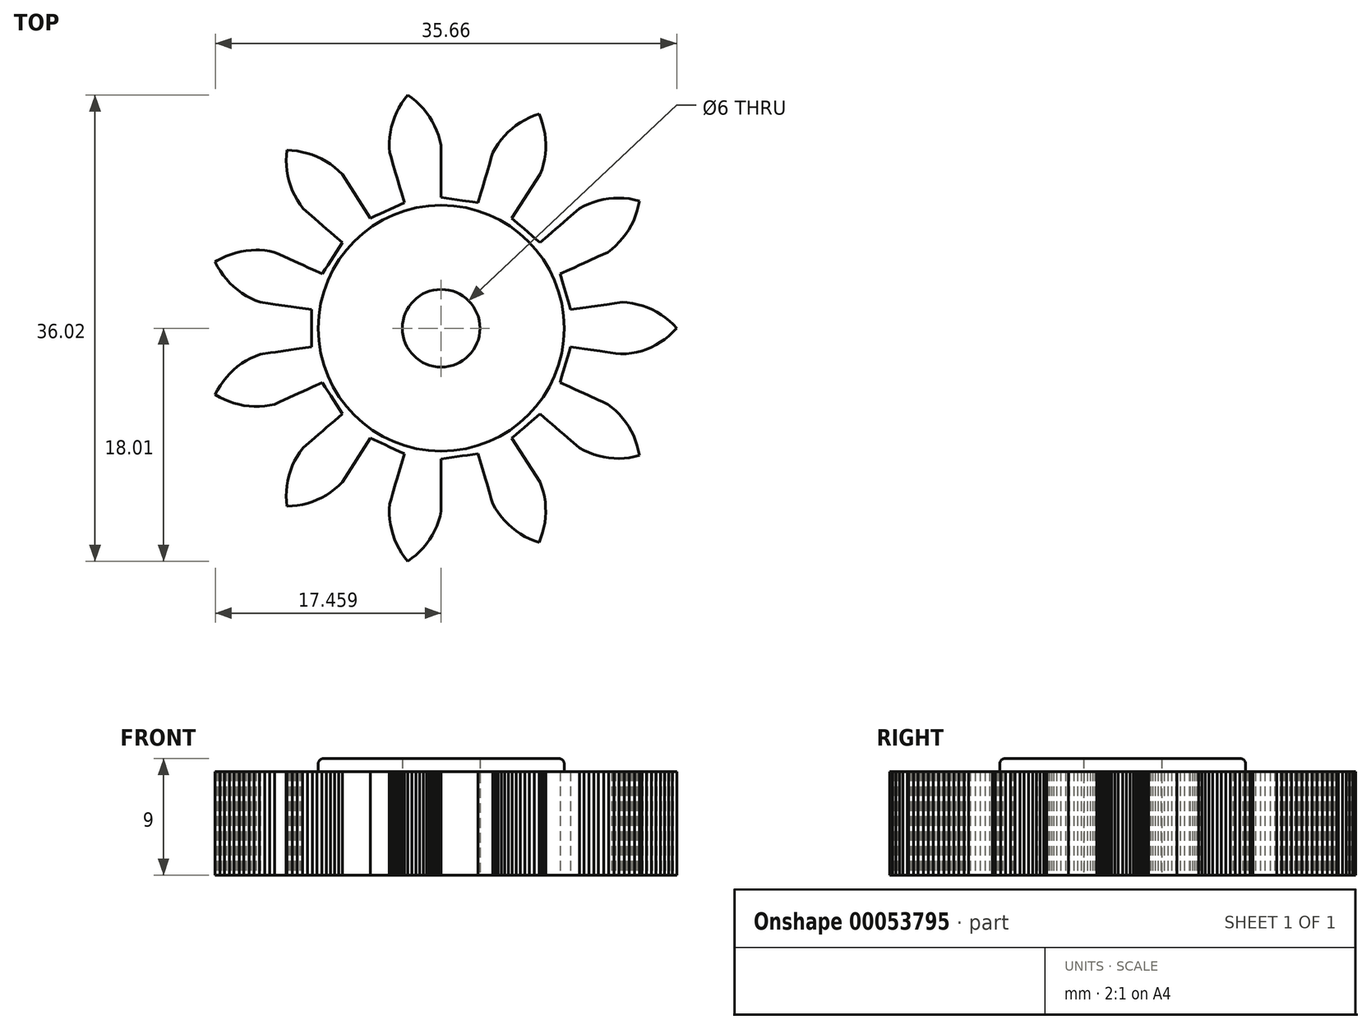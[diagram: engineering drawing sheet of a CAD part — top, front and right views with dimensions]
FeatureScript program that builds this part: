
annotation { "Feature Type Name" : "Feature", "Feature Type Description" : "" }
export const myFeature = defineFeature(function(context is Context, id is Id, definition is map)
    precondition{}
    {
        {
            var Q0;
            Q0=qCreatedBy(makeId("Top.planeOp"),FACE);
            var sketch = newSketch(context, id + "F0", { "sketchPlane" : qUnion([Q0])});
            skLineSegment(sketch, "E0", {"start": v(7.14, -1.44) * mm, "end": v(7.4, -1.48) * mm});
            skLineSegment(sketch, "E1", {"start": v(7.4, -1.48) * mm, "end": v(7.8, -1.53) * mm});
            skLineSegment(sketch, "E2", {"start": v(7.8, -1.53) * mm, "end": v(8.2, -1.6) * mm});
            skLineSegment(sketch, "E3", {"start": v(8.2, -1.6) * mm, "end": v(8.6, -1.65) * mm});
            skLineSegment(sketch, "E4", {"start": v(8.6, -1.65) * mm, "end": v(9, -1.7) * mm});
            skLineSegment(sketch, "E5", {"start": v(9, -1.7) * mm, "end": v(9.4, -1.76) * mm});
            skLineSegment(sketch, "E6", {"start": v(9.4, -1.76) * mm, "end": v(9.8, -1.82) * mm});
            skLineSegment(sketch, "E7", {"start": v(9.8, -1.82) * mm, "end": v(10.2, -1.88) * mm});
            skLineSegment(sketch, "E8", {"start": v(10.2, -1.88) * mm, "end": v(10.6, -1.94) * mm});
            skLineSegment(sketch, "E9", {"start": v(10.6, -1.94) * mm, "end": v(11, -2) * mm});
            skLineSegment(sketch, "E10", {"start": v(11, -2) * mm, "end": v(11.46, -1.99) * mm});
            skLineSegment(sketch, "E11", {"start": v(11.46, -1.99) * mm, "end": v(11.86, -1.93) * mm});
            skLineSegment(sketch, "E12", {"start": v(11.86, -1.93) * mm, "end": v(12.24, -1.86) * mm});
            skLineSegment(sketch, "E13", {"start": v(12.24, -1.86) * mm, "end": v(12.64, -1.75) * mm});
            skLineSegment(sketch, "E14", {"start": v(12.64, -1.75) * mm, "end": v(13, -1.62) * mm});
            skLineSegment(sketch, "E15", {"start": v(13, -1.62) * mm, "end": v(13.38, -1.46) * mm});
            skLineSegment(sketch, "E16", {"start": v(13.38, -1.46) * mm, "end": v(13.73, -1.29) * mm});
            skLineSegment(sketch, "E17", {"start": v(13.73, -1.29) * mm, "end": v(14.08, -1.08) * mm});
            skLineSegment(sketch, "E18", {"start": v(14.08, -1.08) * mm, "end": v(14.4, -0.86) * mm});
            skLineSegment(sketch, "E19", {"start": v(14.4, -0.86) * mm, "end": v(14.72, -0.6) * mm});
            skLineSegment(sketch, "E20", {"start": v(14.72, -0.6) * mm, "end": v(15, -0.35) * mm});
            skLineSegment(sketch, "E21", {"start": v(15, -0.35) * mm, "end": v(15.3, -0.05) * mm});
            skLineSegment(sketch, "E22", {"start": v(15.3, -0.05) * mm, "end": v(15.34, 0) * mm});
            skLineSegment(sketch, "E23", {"start": v(15.34, 0) * mm, "end": v(15.05, 0.3) * mm});
            skLineSegment(sketch, "E24", {"start": v(15.05, 0.3) * mm, "end": v(14.77, 0.56) * mm});
            skLineSegment(sketch, "E25", {"start": v(14.77, 0.56) * mm, "end": v(14.45, 0.82) * mm});
            skLineSegment(sketch, "E26", {"start": v(14.45, 0.82) * mm, "end": v(14.14, 1.04) * mm});
            skLineSegment(sketch, "E27", {"start": v(14.14, 1.04) * mm, "end": v(13.78, 1.25) * mm});
            skLineSegment(sketch, "E28", {"start": v(13.78, 1.25) * mm, "end": v(13.44, 1.43) * mm});
            skLineSegment(sketch, "E29", {"start": v(13.44, 1.43) * mm, "end": v(13.07, 1.6) * mm});
            skLineSegment(sketch, "E30", {"start": v(13.07, 1.6) * mm, "end": v(12.7, 1.73) * mm});
            skLineSegment(sketch, "E31", {"start": v(12.7, 1.73) * mm, "end": v(12.3, 1.84) * mm});
            skLineSegment(sketch, "E32", {"start": v(12.3, 1.84) * mm, "end": v(11.93, 1.92) * mm});
            skLineSegment(sketch, "E33", {"start": v(11.93, 1.92) * mm, "end": v(11.52, 1.98) * mm});
            skLineSegment(sketch, "E34", {"start": v(11.52, 1.98) * mm, "end": v(11.14, 2.01) * mm});
            skLineSegment(sketch, "E35", {"start": v(11.14, 2.01) * mm, "end": v(10.74, 1.96) * mm});
            skLineSegment(sketch, "E36", {"start": v(10.74, 1.96) * mm, "end": v(10.34, 1.9) * mm});
            skLineSegment(sketch, "E37", {"start": v(10.34, 1.9) * mm, "end": v(9.94, 1.84) * mm});
            skLineSegment(sketch, "E38", {"start": v(9.94, 1.84) * mm, "end": v(9.54, 1.78) * mm});
            skLineSegment(sketch, "E39", {"start": v(9.54, 1.78) * mm, "end": v(9.14, 1.73) * mm});
            skLineSegment(sketch, "E40", {"start": v(9.14, 1.73) * mm, "end": v(8.74, 1.67) * mm});
            skLineSegment(sketch, "E41", {"start": v(8.74, 1.67) * mm, "end": v(8.34, 1.61) * mm});
            skLineSegment(sketch, "E42", {"start": v(8.34, 1.61) * mm, "end": v(7.94, 1.55) * mm});
            skLineSegment(sketch, "E43", {"start": v(7.94, 1.55) * mm, "end": v(7.54, 1.5) * mm});
            skLineSegment(sketch, "E44", {"start": v(7.54, 1.5) * mm, "end": v(7.14, 1.44) * mm});
            skLineSegment(sketch, "E45", {"start": v(7.14, 1.44) * mm, "end": v(7.02, 1.83) * mm});
            skLineSegment(sketch, "E46", {"start": v(7.02, 1.83) * mm, "end": v(6.9, 2.23) * mm});
            skLineSegment(sketch, "E47", {"start": v(6.9, 2.23) * mm, "end": v(6.8, 2.62) * mm});
            skLineSegment(sketch, "E48", {"start": v(6.8, 2.62) * mm, "end": v(6.68, 3.01) * mm});
            skLineSegment(sketch, "E49", {"start": v(6.68, 3.01) * mm, "end": v(6.56, 3.4) * mm});
            skLineSegment(sketch, "E50", {"start": v(6.56, 3.4) * mm, "end": v(6.45, 3.8) * mm});
            skLineSegment(sketch, "E51", {"start": v(6.45, 3.8) * mm, "end": v(6.33, 4.2) * mm});
            skLineSegment(sketch, "E52", {"start": v(6.33, 4.2) * mm, "end": v(6.7, 4.36) * mm});
            skLineSegment(sketch, "E53", {"start": v(6.7, 4.36) * mm, "end": v(7.06, 4.53) * mm});
            skLineSegment(sketch, "E54", {"start": v(7.06, 4.53) * mm, "end": v(7.43, 4.7) * mm});
            skLineSegment(sketch, "E55", {"start": v(7.43, 4.7) * mm, "end": v(7.8, 4.87) * mm});
            skLineSegment(sketch, "E56", {"start": v(7.8, 4.87) * mm, "end": v(8.17, 5.04) * mm});
            skLineSegment(sketch, "E57", {"start": v(8.17, 5.04) * mm, "end": v(8.53, 5.2) * mm});
            skLineSegment(sketch, "E58", {"start": v(8.53, 5.2) * mm, "end": v(8.9, 5.37) * mm});
            skLineSegment(sketch, "E59", {"start": v(8.9, 5.37) * mm, "end": v(9.27, 5.54) * mm});
            skLineSegment(sketch, "E60", {"start": v(9.27, 5.54) * mm, "end": v(9.64, 5.7) * mm});
            skLineSegment(sketch, "E61", {"start": v(9.64, 5.7) * mm, "end": v(10, 5.87) * mm});
            skLineSegment(sketch, "E62", {"start": v(10, 5.87) * mm, "end": v(10.33, 6.13) * mm});
            skLineSegment(sketch, "E63", {"start": v(10.33, 6.13) * mm, "end": v(10.62, 6.38) * mm});
            skLineSegment(sketch, "E64", {"start": v(10.62, 6.38) * mm, "end": v(10.9, 6.67) * mm});
            skLineSegment(sketch, "E65", {"start": v(10.9, 6.67) * mm, "end": v(11.17, 6.96) * mm});
            skLineSegment(sketch, "E66", {"start": v(11.17, 6.96) * mm, "end": v(11.41, 7.29) * mm});
            skLineSegment(sketch, "E67", {"start": v(11.41, 7.29) * mm, "end": v(11.63, 7.6) * mm});
            skLineSegment(sketch, "E68", {"start": v(11.63, 7.6) * mm, "end": v(11.83, 7.97) * mm});
            skLineSegment(sketch, "E69", {"start": v(11.83, 7.97) * mm, "end": v(12, 8.31) * mm});
            skLineSegment(sketch, "E70", {"start": v(12, 8.31) * mm, "end": v(12.15, 8.7) * mm});
            skLineSegment(sketch, "E71", {"start": v(12.15, 8.7) * mm, "end": v(12.28, 9.06) * mm});
            skLineSegment(sketch, "E72", {"start": v(12.28, 9.06) * mm, "end": v(12.38, 9.46) * mm});
            skLineSegment(sketch, "E73", {"start": v(12.38, 9.46) * mm, "end": v(12.45, 9.84) * mm});
            skLineSegment(sketch, "E74", {"start": v(12.45, 9.84) * mm, "end": v(12.05, 9.94) * mm});
            skLineSegment(sketch, "E75", {"start": v(12.05, 9.94) * mm, "end": v(11.67, 10) * mm});
            skLineSegment(sketch, "E76", {"start": v(11.67, 10) * mm, "end": v(11.26, 10.05) * mm});
            skLineSegment(sketch, "E77", {"start": v(11.26, 10.05) * mm, "end": v(10.88, 10.06) * mm});
            skLineSegment(sketch, "E78", {"start": v(10.88, 10.06) * mm, "end": v(10.47, 10.05) * mm});
            skLineSegment(sketch, "E79", {"start": v(10.47, 10.05) * mm, "end": v(10.08, 10.02) * mm});
            skLineSegment(sketch, "E80", {"start": v(10.08, 10.02) * mm, "end": v(9.67, 9.95) * mm});
            skLineSegment(sketch, "E81", {"start": v(9.67, 9.95) * mm, "end": v(9.3, 9.87) * mm});
            skLineSegment(sketch, "E82", {"start": v(9.3, 9.87) * mm, "end": v(8.9, 9.75) * mm});
            skLineSegment(sketch, "E83", {"start": v(8.9, 9.75) * mm, "end": v(8.54, 9.61) * mm});
            skLineSegment(sketch, "E84", {"start": v(8.54, 9.61) * mm, "end": v(8.17, 9.44) * mm});
            skLineSegment(sketch, "E85", {"start": v(8.17, 9.44) * mm, "end": v(7.83, 9.26) * mm});
            skLineSegment(sketch, "E86", {"start": v(7.83, 9.26) * mm, "end": v(7.52, 9) * mm});
            skLineSegment(sketch, "E87", {"start": v(7.52, 9) * mm, "end": v(7.22, 8.73) * mm});
            skLineSegment(sketch, "E88", {"start": v(7.22, 8.73) * mm, "end": v(6.91, 8.47) * mm});
            skLineSegment(sketch, "E89", {"start": v(6.91, 8.47) * mm, "end": v(6.6, 8.2) * mm});
            skLineSegment(sketch, "E90", {"start": v(6.6, 8.2) * mm, "end": v(6.3, 7.94) * mm});
            skLineSegment(sketch, "E91", {"start": v(6.3, 7.94) * mm, "end": v(6, 7.67) * mm});
            skLineSegment(sketch, "E92", {"start": v(6, 7.67) * mm, "end": v(5.7, 7.4) * mm});
            skLineSegment(sketch, "E93", {"start": v(5.7, 7.4) * mm, "end": v(5.39, 7.15) * mm});
            skLineSegment(sketch, "E94", {"start": v(5.39, 7.15) * mm, "end": v(5.08, 6.88) * mm});
            skLineSegment(sketch, "E95", {"start": v(5.08, 6.88) * mm, "end": v(4.77, 6.62) * mm});
            skLineSegment(sketch, "E96", {"start": v(4.77, 6.62) * mm, "end": v(4.46, 6.88) * mm});
            skLineSegment(sketch, "E97", {"start": v(4.46, 6.88) * mm, "end": v(4.15, 7.15) * mm});
            skLineSegment(sketch, "E98", {"start": v(4.15, 7.15) * mm, "end": v(3.84, 7.42) * mm});
            skLineSegment(sketch, "E99", {"start": v(3.84, 7.42) * mm, "end": v(3.53, 7.7) * mm});
            skLineSegment(sketch, "E100", {"start": v(3.53, 7.7) * mm, "end": v(3.22, 7.96) * mm});
            skLineSegment(sketch, "E101", {"start": v(3.22, 7.96) * mm, "end": v(2.91, 8.23) * mm});
            skLineSegment(sketch, "E102", {"start": v(2.91, 8.23) * mm, "end": v(2.6, 8.5) * mm});
            skLineSegment(sketch, "E103", {"start": v(2.6, 8.5) * mm, "end": v(2.82, 8.84) * mm});
            skLineSegment(sketch, "E104", {"start": v(2.82, 8.84) * mm, "end": v(3.04, 9.18) * mm});
            skLineSegment(sketch, "E105", {"start": v(3.04, 9.18) * mm, "end": v(3.26, 9.52) * mm});
            skLineSegment(sketch, "E106", {"start": v(3.26, 9.52) * mm, "end": v(3.48, 9.86) * mm});
            skLineSegment(sketch, "E107", {"start": v(3.48, 9.86) * mm, "end": v(3.7, 10.2) * mm});
            skLineSegment(sketch, "E108", {"start": v(3.7, 10.2) * mm, "end": v(3.91, 10.54) * mm});
            skLineSegment(sketch, "E109", {"start": v(3.91, 10.54) * mm, "end": v(4.13, 10.88) * mm});
            skLineSegment(sketch, "E110", {"start": v(4.13, 10.88) * mm, "end": v(4.35, 11.22) * mm});
            skLineSegment(sketch, "E111", {"start": v(4.35, 11.22) * mm, "end": v(4.57, 11.56) * mm});
            skLineSegment(sketch, "E112", {"start": v(4.57, 11.56) * mm, "end": v(4.79, 11.9) * mm});
            skLineSegment(sketch, "E113", {"start": v(4.79, 11.9) * mm, "end": v(4.92, 12.28) * mm});
            skLineSegment(sketch, "E114", {"start": v(4.92, 12.28) * mm, "end": v(5.03, 12.65) * mm});
            skLineSegment(sketch, "E115", {"start": v(5.03, 12.65) * mm, "end": v(5.12, 13.06) * mm});
            skLineSegment(sketch, "E116", {"start": v(5.12, 13.06) * mm, "end": v(5.18, 13.44) * mm});
            skLineSegment(sketch, "E117", {"start": v(5.18, 13.44) * mm, "end": v(5.2, 13.85) * mm});
            skLineSegment(sketch, "E118", {"start": v(5.2, 13.85) * mm, "end": v(5.21, 14.23) * mm});
            skLineSegment(sketch, "E119", {"start": v(5.21, 14.23) * mm, "end": v(5.2, 14.64) * mm});
            skLineSegment(sketch, "E120", {"start": v(5.2, 14.64) * mm, "end": v(5.15, 15.03) * mm});
            skLineSegment(sketch, "E121", {"start": v(5.15, 15.03) * mm, "end": v(5.07, 15.43) * mm});
            skLineSegment(sketch, "E122", {"start": v(5.07, 15.43) * mm, "end": v(4.97, 15.8) * mm});
            skLineSegment(sketch, "E123", {"start": v(4.97, 15.8) * mm, "end": v(4.84, 16.2) * mm});
            skLineSegment(sketch, "E124", {"start": v(4.84, 16.2) * mm, "end": v(4.7, 16.55) * mm});
            skLineSegment(sketch, "E125", {"start": v(4.7, 16.55) * mm, "end": v(4.31, 16.42) * mm});
            skLineSegment(sketch, "E126", {"start": v(4.31, 16.42) * mm, "end": v(3.95, 16.27) * mm});
            skLineSegment(sketch, "E127", {"start": v(3.95, 16.27) * mm, "end": v(3.59, 16.09) * mm});
            skLineSegment(sketch, "E128", {"start": v(3.59, 16.09) * mm, "end": v(3.25, 15.9) * mm});
            skLineSegment(sketch, "E129", {"start": v(3.25, 15.9) * mm, "end": v(2.92, 15.66) * mm});
            skLineSegment(sketch, "E130", {"start": v(2.92, 15.66) * mm, "end": v(2.6, 15.42) * mm});
            skLineSegment(sketch, "E131", {"start": v(2.6, 15.42) * mm, "end": v(2.3, 15.15) * mm});
            skLineSegment(sketch, "E132", {"start": v(2.3, 15.15) * mm, "end": v(2.03, 14.87) * mm});
            skLineSegment(sketch, "E133", {"start": v(2.03, 14.87) * mm, "end": v(1.77, 14.56) * mm});
            skLineSegment(sketch, "E134", {"start": v(1.77, 14.56) * mm, "end": v(1.53, 14.25) * mm});
            skLineSegment(sketch, "E135", {"start": v(1.53, 14.25) * mm, "end": v(1.31, 13.9) * mm});
            skLineSegment(sketch, "E136", {"start": v(1.31, 13.9) * mm, "end": v(1.12, 13.57) * mm});
            skLineSegment(sketch, "E137", {"start": v(1.12, 13.57) * mm, "end": v(1.01, 13.18) * mm});
            skLineSegment(sketch, "E138", {"start": v(1.01, 13.18) * mm, "end": v(0.9, 12.8) * mm});
            skLineSegment(sketch, "E139", {"start": v(0.9, 12.8) * mm, "end": v(0.78, 12.4) * mm});
            skLineSegment(sketch, "E140", {"start": v(0.78, 12.4) * mm, "end": v(0.67, 12.02) * mm});
            skLineSegment(sketch, "E141", {"start": v(0.67, 12.02) * mm, "end": v(0.55, 11.63) * mm});
            skLineSegment(sketch, "E142", {"start": v(0.55, 11.63) * mm, "end": v(0.44, 11.24) * mm});
            skLineSegment(sketch, "E143", {"start": v(0.44, 11.24) * mm, "end": v(0.33, 10.86) * mm});
            skLineSegment(sketch, "E144", {"start": v(0.33, 10.86) * mm, "end": v(0.21, 10.47) * mm});
            skLineSegment(sketch, "E145", {"start": v(0.21, 10.47) * mm, "end": v(0.1, 10.08) * mm});
            skLineSegment(sketch, "E146", {"start": v(0.1, 10.08) * mm, "end": v(-0.01, 9.7) * mm});
            skLineSegment(sketch, "E147", {"start": v(-0.01, 9.7) * mm, "end": v(-0.42, 9.75) * mm});
            skLineSegment(sketch, "E148", {"start": v(-0.42, 9.75) * mm, "end": v(-0.83, 9.81) * mm});
            skLineSegment(sketch, "E149", {"start": v(-0.83, 9.81) * mm, "end": v(-1.23, 9.87) * mm});
            skLineSegment(sketch, "E150", {"start": v(-1.23, 9.87) * mm, "end": v(-1.64, 9.93) * mm});
            skLineSegment(sketch, "E151", {"start": v(-1.64, 9.93) * mm, "end": v(-2.05, 9.99) * mm});
            skLineSegment(sketch, "E152", {"start": v(-2.05, 9.99) * mm, "end": v(-2.45, 10.04) * mm});
            skLineSegment(sketch, "E153", {"start": v(-2.45, 10.04) * mm, "end": v(-2.86, 10.1) * mm});
            skLineSegment(sketch, "E154", {"start": v(-2.86, 10.1) * mm, "end": v(-2.86, 10.5) * mm});
            skLineSegment(sketch, "E155", {"start": v(-2.86, 10.5) * mm, "end": v(-2.86, 10.91) * mm});
            skLineSegment(sketch, "E156", {"start": v(-2.86, 10.91) * mm, "end": v(-2.86, 11.31) * mm});
            skLineSegment(sketch, "E157", {"start": v(-2.86, 11.31) * mm, "end": v(-2.86, 11.72) * mm});
            skLineSegment(sketch, "E158", {"start": v(-2.86, 11.72) * mm, "end": v(-2.86, 12.12) * mm});
            skLineSegment(sketch, "E159", {"start": v(-2.86, 12.12) * mm, "end": v(-2.86, 12.53) * mm});
            skLineSegment(sketch, "E160", {"start": v(-2.86, 12.53) * mm, "end": v(-2.86, 12.93) * mm});
            skLineSegment(sketch, "E161", {"start": v(-2.86, 12.93) * mm, "end": v(-2.86, 13.33) * mm});
            skLineSegment(sketch, "E162", {"start": v(-2.86, 13.33) * mm, "end": v(-2.86, 13.74) * mm});
            skLineSegment(sketch, "E163", {"start": v(-2.86, 13.74) * mm, "end": v(-2.86, 14.14) * mm});
            skLineSegment(sketch, "E164", {"start": v(-2.86, 14.14) * mm, "end": v(-2.95, 14.54) * mm});
            skLineSegment(sketch, "E165", {"start": v(-2.95, 14.54) * mm, "end": v(-3.06, 14.91) * mm});
            skLineSegment(sketch, "E166", {"start": v(-3.06, 14.91) * mm, "end": v(-3.2, 15.3) * mm});
            skLineSegment(sketch, "E167", {"start": v(-3.2, 15.3) * mm, "end": v(-3.36, 15.65) * mm});
            skLineSegment(sketch, "E168", {"start": v(-3.36, 15.65) * mm, "end": v(-3.56, 16.01) * mm});
            skLineSegment(sketch, "E169", {"start": v(-3.56, 16.01) * mm, "end": v(-3.76, 16.34) * mm});
            skLineSegment(sketch, "E170", {"start": v(-3.76, 16.34) * mm, "end": v(-4, 16.67) * mm});
            skLineSegment(sketch, "E171", {"start": v(-4, 16.67) * mm, "end": v(-4.25, 16.97) * mm});
            skLineSegment(sketch, "E172", {"start": v(-4.25, 16.97) * mm, "end": v(-4.53, 17.27) * mm});
            skLineSegment(sketch, "E173", {"start": v(-4.53, 17.27) * mm, "end": v(-4.82, 17.53) * mm});
            skLineSegment(sketch, "E174", {"start": v(-4.82, 17.53) * mm, "end": v(-5.14, 17.79) * mm});
            skLineSegment(sketch, "E175", {"start": v(-5.14, 17.79) * mm, "end": v(-5.45, 18.01) * mm});
            skLineSegment(sketch, "E176", {"start": v(-5.45, 18.01) * mm, "end": v(-5.7, 17.7) * mm});
            skLineSegment(sketch, "E177", {"start": v(-5.7, 17.7) * mm, "end": v(-5.92, 17.37) * mm});
            skLineSegment(sketch, "E178", {"start": v(-5.92, 17.37) * mm, "end": v(-6.13, 17.02) * mm});
            skLineSegment(sketch, "E179", {"start": v(-6.13, 17.02) * mm, "end": v(-6.3, 16.68) * mm});
            skLineSegment(sketch, "E180", {"start": v(-6.3, 16.68) * mm, "end": v(-6.47, 16.3) * mm});
            skLineSegment(sketch, "E181", {"start": v(-6.47, 16.3) * mm, "end": v(-6.6, 15.93) * mm});
            skLineSegment(sketch, "E182", {"start": v(-6.6, 15.93) * mm, "end": v(-6.7, 15.54) * mm});
            skLineSegment(sketch, "E183", {"start": v(-6.7, 15.54) * mm, "end": v(-6.79, 15.16) * mm});
            skLineSegment(sketch, "E184", {"start": v(-6.79, 15.16) * mm, "end": v(-6.84, 14.75) * mm});
            skLineSegment(sketch, "E185", {"start": v(-6.84, 14.75) * mm, "end": v(-6.87, 14.37) * mm});
            skLineSegment(sketch, "E186", {"start": v(-6.87, 14.37) * mm, "end": v(-6.87, 13.96) * mm});
            skLineSegment(sketch, "E187", {"start": v(-6.87, 13.96) * mm, "end": v(-6.84, 13.57) * mm});
            skLineSegment(sketch, "E188", {"start": v(-6.84, 13.57) * mm, "end": v(-6.73, 13.18) * mm});
            skLineSegment(sketch, "E189", {"start": v(-6.73, 13.18) * mm, "end": v(-6.62, 12.8) * mm});
            skLineSegment(sketch, "E190", {"start": v(-6.62, 12.8) * mm, "end": v(-6.5, 12.4) * mm});
            skLineSegment(sketch, "E191", {"start": v(-6.5, 12.4) * mm, "end": v(-6.39, 12.02) * mm});
            skLineSegment(sketch, "E192", {"start": v(-6.39, 12.02) * mm, "end": v(-6.28, 11.63) * mm});
            skLineSegment(sketch, "E193", {"start": v(-6.28, 11.63) * mm, "end": v(-6.16, 11.24) * mm});
            skLineSegment(sketch, "E194", {"start": v(-6.16, 11.24) * mm, "end": v(-6.05, 10.86) * mm});
            skLineSegment(sketch, "E195", {"start": v(-6.05, 10.86) * mm, "end": v(-5.93, 10.47) * mm});
            skLineSegment(sketch, "E196", {"start": v(-5.93, 10.47) * mm, "end": v(-5.82, 10.08) * mm});
            skLineSegment(sketch, "E197", {"start": v(-5.82, 10.08) * mm, "end": v(-5.7, 9.7) * mm});
            skLineSegment(sketch, "E198", {"start": v(-5.7, 9.7) * mm, "end": v(-6.08, 9.52) * mm});
            skLineSegment(sketch, "E199", {"start": v(-6.08, 9.52) * mm, "end": v(-6.45, 9.35) * mm});
            skLineSegment(sketch, "E200", {"start": v(-6.45, 9.35) * mm, "end": v(-6.83, 9.18) * mm});
            skLineSegment(sketch, "E201", {"start": v(-6.83, 9.18) * mm, "end": v(-7.2, 9.01) * mm});
            skLineSegment(sketch, "E202", {"start": v(-7.2, 9.01) * mm, "end": v(-7.57, 8.84) * mm});
            skLineSegment(sketch, "E203", {"start": v(-7.57, 8.84) * mm, "end": v(-7.95, 8.67) * mm});
            skLineSegment(sketch, "E204", {"start": v(-7.95, 8.67) * mm, "end": v(-8.32, 8.5) * mm});
            skLineSegment(sketch, "E205", {"start": v(-8.32, 8.5) * mm, "end": v(-8.54, 8.84) * mm});
            skLineSegment(sketch, "E206", {"start": v(-8.54, 8.84) * mm, "end": v(-8.76, 9.18) * mm});
            skLineSegment(sketch, "E207", {"start": v(-8.76, 9.18) * mm, "end": v(-8.98, 9.52) * mm});
            skLineSegment(sketch, "E208", {"start": v(-8.98, 9.52) * mm, "end": v(-9.2, 9.86) * mm});
            skLineSegment(sketch, "E209", {"start": v(-9.2, 9.86) * mm, "end": v(-9.41, 10.2) * mm});
            skLineSegment(sketch, "E210", {"start": v(-9.41, 10.2) * mm, "end": v(-9.63, 10.54) * mm});
            skLineSegment(sketch, "E211", {"start": v(-9.63, 10.54) * mm, "end": v(-9.85, 10.88) * mm});
            skLineSegment(sketch, "E212", {"start": v(-9.85, 10.88) * mm, "end": v(-10.07, 11.22) * mm});
            skLineSegment(sketch, "E213", {"start": v(-10.07, 11.22) * mm, "end": v(-10.29, 11.56) * mm});
            skLineSegment(sketch, "E214", {"start": v(-10.29, 11.56) * mm, "end": v(-10.5, 11.9) * mm});
            skLineSegment(sketch, "E215", {"start": v(-10.5, 11.9) * mm, "end": v(-10.8, 12.18) * mm});
            skLineSegment(sketch, "E216", {"start": v(-10.8, 12.18) * mm, "end": v(-11.1, 12.44) * mm});
            skLineSegment(sketch, "E217", {"start": v(-11.1, 12.44) * mm, "end": v(-11.42, 12.68) * mm});
            skLineSegment(sketch, "E218", {"start": v(-11.42, 12.68) * mm, "end": v(-11.75, 12.9) * mm});
            skLineSegment(sketch, "E219", {"start": v(-11.75, 12.9) * mm, "end": v(-12.1, 13.1) * mm});
            skLineSegment(sketch, "E220", {"start": v(-12.1, 13.1) * mm, "end": v(-12.45, 13.26) * mm});
            skLineSegment(sketch, "E221", {"start": v(-12.45, 13.26) * mm, "end": v(-12.84, 13.4) * mm});
            skLineSegment(sketch, "E222", {"start": v(-12.84, 13.4) * mm, "end": v(-13.2, 13.53) * mm});
            skLineSegment(sketch, "E223", {"start": v(-13.2, 13.53) * mm, "end": v(-13.6, 13.62) * mm});
            skLineSegment(sketch, "E224", {"start": v(-13.6, 13.62) * mm, "end": v(-13.98, 13.7) * mm});
            skLineSegment(sketch, "E225", {"start": v(-13.98, 13.7) * mm, "end": v(-14.4, 13.74) * mm});
            skLineSegment(sketch, "E226", {"start": v(-14.4, 13.74) * mm, "end": v(-14.78, 13.75) * mm});
            skLineSegment(sketch, "E227", {"start": v(-14.78, 13.75) * mm, "end": v(-14.82, 13.35) * mm});
            skLineSegment(sketch, "E228", {"start": v(-14.82, 13.35) * mm, "end": v(-14.83, 12.96) * mm});
            skLineSegment(sketch, "E229", {"start": v(-14.83, 12.96) * mm, "end": v(-14.81, 12.55) * mm});
            skLineSegment(sketch, "E230", {"start": v(-14.81, 12.55) * mm, "end": v(-14.78, 12.16) * mm});
            skLineSegment(sketch, "E231", {"start": v(-14.78, 12.16) * mm, "end": v(-14.7, 11.76) * mm});
            skLineSegment(sketch, "E232", {"start": v(-14.7, 11.76) * mm, "end": v(-14.62, 11.38) * mm});
            skLineSegment(sketch, "E233", {"start": v(-14.62, 11.38) * mm, "end": v(-14.5, 11) * mm});
            skLineSegment(sketch, "E234", {"start": v(-14.5, 11) * mm, "end": v(-14.36, 10.63) * mm});
            skLineSegment(sketch, "E235", {"start": v(-14.36, 10.63) * mm, "end": v(-14.18, 10.26) * mm});
            skLineSegment(sketch, "E236", {"start": v(-14.18, 10.26) * mm, "end": v(-14, 9.92) * mm});
            skLineSegment(sketch, "E237", {"start": v(-14, 9.92) * mm, "end": v(-13.78, 9.57) * mm});
            skLineSegment(sketch, "E238", {"start": v(-13.78, 9.57) * mm, "end": v(-13.55, 9.26) * mm});
            skLineSegment(sketch, "E239", {"start": v(-13.55, 9.26) * mm, "end": v(-13.24, 9) * mm});
            skLineSegment(sketch, "E240", {"start": v(-13.24, 9) * mm, "end": v(-12.94, 8.73) * mm});
            skLineSegment(sketch, "E241", {"start": v(-12.94, 8.73) * mm, "end": v(-12.63, 8.47) * mm});
            skLineSegment(sketch, "E242", {"start": v(-12.63, 8.47) * mm, "end": v(-12.33, 8.2) * mm});
            skLineSegment(sketch, "E243", {"start": v(-12.33, 8.2) * mm, "end": v(-12.02, 7.94) * mm});
            skLineSegment(sketch, "E244", {"start": v(-12.02, 7.94) * mm, "end": v(-11.72, 7.67) * mm});
            skLineSegment(sketch, "E245", {"start": v(-11.72, 7.67) * mm, "end": v(-11.41, 7.4) * mm});
            skLineSegment(sketch, "E246", {"start": v(-11.41, 7.4) * mm, "end": v(-11.1, 7.15) * mm});
            skLineSegment(sketch, "E247", {"start": v(-11.1, 7.15) * mm, "end": v(-10.8, 6.88) * mm});
            skLineSegment(sketch, "E248", {"start": v(-10.8, 6.88) * mm, "end": v(-10.5, 6.62) * mm});
            skLineSegment(sketch, "E249", {"start": v(-10.5, 6.62) * mm, "end": v(-10.72, 6.27) * mm});
            skLineSegment(sketch, "E250", {"start": v(-10.72, 6.27) * mm, "end": v(-10.94, 5.93) * mm});
            skLineSegment(sketch, "E251", {"start": v(-10.94, 5.93) * mm, "end": v(-11.16, 5.58) * mm});
            skLineSegment(sketch, "E252", {"start": v(-11.16, 5.58) * mm, "end": v(-11.38, 5.23) * mm});
            skLineSegment(sketch, "E253", {"start": v(-11.38, 5.23) * mm, "end": v(-11.6, 4.89) * mm});
            skLineSegment(sketch, "E254", {"start": v(-11.6, 4.89) * mm, "end": v(-11.83, 4.54) * mm});
            skLineSegment(sketch, "E255", {"start": v(-11.83, 4.54) * mm, "end": v(-12.05, 4.2) * mm});
            skLineSegment(sketch, "E256", {"start": v(-12.05, 4.2) * mm, "end": v(-12.42, 4.36) * mm});
            skLineSegment(sketch, "E257", {"start": v(-12.42, 4.36) * mm, "end": v(-12.79, 4.53) * mm});
            skLineSegment(sketch, "E258", {"start": v(-12.79, 4.53) * mm, "end": v(-13.15, 4.7) * mm});
            skLineSegment(sketch, "E259", {"start": v(-13.15, 4.7) * mm, "end": v(-13.52, 4.87) * mm});
            skLineSegment(sketch, "E260", {"start": v(-13.52, 4.87) * mm, "end": v(-13.89, 5.04) * mm});
            skLineSegment(sketch, "E261", {"start": v(-13.89, 5.04) * mm, "end": v(-14.26, 5.2) * mm});
            skLineSegment(sketch, "E262", {"start": v(-14.26, 5.2) * mm, "end": v(-14.62, 5.37) * mm});
            skLineSegment(sketch, "E263", {"start": v(-14.62, 5.37) * mm, "end": v(-14.99, 5.54) * mm});
            skLineSegment(sketch, "E264", {"start": v(-14.99, 5.54) * mm, "end": v(-15.36, 5.7) * mm});
            skLineSegment(sketch, "E265", {"start": v(-15.36, 5.7) * mm, "end": v(-15.72, 5.87) * mm});
            skLineSegment(sketch, "E266", {"start": v(-15.72, 5.87) * mm, "end": v(-16.13, 5.96) * mm});
            skLineSegment(sketch, "E267", {"start": v(-16.13, 5.96) * mm, "end": v(-16.5, 6.01) * mm});
            skLineSegment(sketch, "E268", {"start": v(-16.5, 6.01) * mm, "end": v(-16.92, 6.04) * mm});
            skLineSegment(sketch, "E269", {"start": v(-16.92, 6.04) * mm, "end": v(-17.15, 6.04) * mm});
            skLineSegment(sketch, "E270", {"start": v(-17.15, 6.04) * mm, "end": v(-17.56, 6.03) * mm});
            skLineSegment(sketch, "E271", {"start": v(-17.56, 6.03) * mm, "end": v(-17.94, 6) * mm});
            skLineSegment(sketch, "E272", {"start": v(-17.94, 6) * mm, "end": v(-18.35, 5.92) * mm});
            skLineSegment(sketch, "E273", {"start": v(-18.35, 5.92) * mm, "end": v(-18.72, 5.83) * mm});
            skLineSegment(sketch, "E274", {"start": v(-18.72, 5.83) * mm, "end": v(-19.11, 5.7) * mm});
            skLineSegment(sketch, "E275", {"start": v(-19.11, 5.7) * mm, "end": v(-19.48, 5.57) * mm});
            skLineSegment(sketch, "E276", {"start": v(-19.48, 5.57) * mm, "end": v(-19.85, 5.4) * mm});
            skLineSegment(sketch, "E277", {"start": v(-19.85, 5.4) * mm, "end": v(-20.19, 5.21) * mm});
            skLineSegment(sketch, "E278", {"start": v(-20.19, 5.21) * mm, "end": v(-20.32, 5.13) * mm});
            skLineSegment(sketch, "E279", {"start": v(-20.32, 5.13) * mm, "end": v(-20.13, 4.76) * mm});
            skLineSegment(sketch, "E280", {"start": v(-20.13, 4.76) * mm, "end": v(-19.94, 4.43) * mm});
            skLineSegment(sketch, "E281", {"start": v(-19.94, 4.43) * mm, "end": v(-19.7, 4.1) * mm});
            skLineSegment(sketch, "E282", {"start": v(-19.7, 4.1) * mm, "end": v(-19.46, 3.79) * mm});
            skLineSegment(sketch, "E283", {"start": v(-19.46, 3.79) * mm, "end": v(-19.18, 3.49) * mm});
            skLineSegment(sketch, "E284", {"start": v(-19.18, 3.49) * mm, "end": v(-18.9, 3.22) * mm});
            skLineSegment(sketch, "E285", {"start": v(-18.9, 3.22) * mm, "end": v(-18.6, 2.96) * mm});
            skLineSegment(sketch, "E286", {"start": v(-18.6, 2.96) * mm, "end": v(-18.28, 2.73) * mm});
            skLineSegment(sketch, "E287", {"start": v(-18.28, 2.73) * mm, "end": v(-17.93, 2.5) * mm});
            skLineSegment(sketch, "E288", {"start": v(-17.93, 2.5) * mm, "end": v(-17.6, 2.32) * mm});
            skLineSegment(sketch, "E289", {"start": v(-17.6, 2.32) * mm, "end": v(-17.22, 2.15) * mm});
            skLineSegment(sketch, "E290", {"start": v(-17.22, 2.15) * mm, "end": v(-16.86, 2.01) * mm});
            skLineSegment(sketch, "E291", {"start": v(-16.86, 2.01) * mm, "end": v(-16.46, 1.96) * mm});
            skLineSegment(sketch, "E292", {"start": v(-16.46, 1.96) * mm, "end": v(-16.06, 1.9) * mm});
            skLineSegment(sketch, "E293", {"start": v(-16.06, 1.9) * mm, "end": v(-15.66, 1.84) * mm});
            skLineSegment(sketch, "E294", {"start": v(-15.66, 1.84) * mm, "end": v(-15.26, 1.78) * mm});
            skLineSegment(sketch, "E295", {"start": v(-15.26, 1.78) * mm, "end": v(-14.86, 1.73) * mm});
            skLineSegment(sketch, "E296", {"start": v(-14.86, 1.73) * mm, "end": v(-14.46, 1.67) * mm});
            skLineSegment(sketch, "E297", {"start": v(-14.46, 1.67) * mm, "end": v(-14.06, 1.61) * mm});
            skLineSegment(sketch, "E298", {"start": v(-14.06, 1.61) * mm, "end": v(-13.66, 1.55) * mm});
            skLineSegment(sketch, "E299", {"start": v(-13.66, 1.55) * mm, "end": v(-13.26, 1.5) * mm});
            skLineSegment(sketch, "E300", {"start": v(-13.26, 1.5) * mm, "end": v(-12.86, 1.44) * mm});
            skLineSegment(sketch, "E301", {"start": v(-12.86, 1.44) * mm, "end": v(-12.86, 1.03) * mm});
            skLineSegment(sketch, "E302", {"start": v(-12.86, 1.03) * mm, "end": v(-12.86, 0.62) * mm});
            skLineSegment(sketch, "E303", {"start": v(-12.86, 0.62) * mm, "end": v(-12.86, 0.2) * mm});
            skLineSegment(sketch, "E304", {"start": v(-12.86, 0.2) * mm, "end": v(-12.86, -0.2) * mm});
            skLineSegment(sketch, "E305", {"start": v(-12.86, -0.2) * mm, "end": v(-12.86, -0.61) * mm});
            skLineSegment(sketch, "E306", {"start": v(-12.86, -0.61) * mm, "end": v(-12.86, -1.02) * mm});
            skLineSegment(sketch, "E307", {"start": v(-12.86, -1.02) * mm, "end": v(-12.86, -1.44) * mm});
            skLineSegment(sketch, "E308", {"start": v(-12.86, -1.44) * mm, "end": v(-13.26, -1.5) * mm});
            skLineSegment(sketch, "E309", {"start": v(-13.26, -1.5) * mm, "end": v(-13.66, -1.55) * mm});
            skLineSegment(sketch, "E310", {"start": v(-13.66, -1.55) * mm, "end": v(-14.06, -1.61) * mm});
            skLineSegment(sketch, "E311", {"start": v(-14.06, -1.61) * mm, "end": v(-14.46, -1.67) * mm});
            skLineSegment(sketch, "E312", {"start": v(-14.46, -1.67) * mm, "end": v(-14.86, -1.73) * mm});
            skLineSegment(sketch, "E313", {"start": v(-14.86, -1.73) * mm, "end": v(-15.26, -1.78) * mm});
            skLineSegment(sketch, "E314", {"start": v(-15.26, -1.78) * mm, "end": v(-15.66, -1.84) * mm});
            skLineSegment(sketch, "E315", {"start": v(-15.66, -1.84) * mm, "end": v(-16.06, -1.9) * mm});
            skLineSegment(sketch, "E316", {"start": v(-16.06, -1.9) * mm, "end": v(-16.46, -1.96) * mm});
            skLineSegment(sketch, "E317", {"start": v(-16.46, -1.96) * mm, "end": v(-16.86, -2.01) * mm});
            skLineSegment(sketch, "E318", {"start": v(-16.86, -2.01) * mm, "end": v(-17.24, -2.16) * mm});
            skLineSegment(sketch, "E319", {"start": v(-17.24, -2.16) * mm, "end": v(-17.6, -2.32) * mm});
            skLineSegment(sketch, "E320", {"start": v(-17.6, -2.32) * mm, "end": v(-17.95, -2.52) * mm});
            skLineSegment(sketch, "E321", {"start": v(-17.95, -2.52) * mm, "end": v(-18.28, -2.73) * mm});
            skLineSegment(sketch, "E322", {"start": v(-18.28, -2.73) * mm, "end": v(-18.6, -2.97) * mm});
            skLineSegment(sketch, "E323", {"start": v(-18.6, -2.97) * mm, "end": v(-18.9, -3.22) * mm});
            skLineSegment(sketch, "E324", {"start": v(-18.9, -3.22) * mm, "end": v(-19.2, -3.5) * mm});
            skLineSegment(sketch, "E325", {"start": v(-19.2, -3.5) * mm, "end": v(-19.46, -3.79) * mm});
            skLineSegment(sketch, "E326", {"start": v(-19.46, -3.79) * mm, "end": v(-19.72, -4.11) * mm});
            skLineSegment(sketch, "E327", {"start": v(-19.72, -4.11) * mm, "end": v(-19.94, -4.43) * mm});
            skLineSegment(sketch, "E328", {"start": v(-19.94, -4.43) * mm, "end": v(-20.14, -4.78) * mm});
            skLineSegment(sketch, "E329", {"start": v(-20.14, -4.78) * mm, "end": v(-20.32, -5.13) * mm});
            skLineSegment(sketch, "E330", {"start": v(-20.32, -5.13) * mm, "end": v(-19.97, -5.33) * mm});
            skLineSegment(sketch, "E331", {"start": v(-19.97, -5.33) * mm, "end": v(-19.62, -5.5) * mm});
            skLineSegment(sketch, "E332", {"start": v(-19.62, -5.5) * mm, "end": v(-19.24, -5.66) * mm});
            skLineSegment(sketch, "E333", {"start": v(-19.24, -5.66) * mm, "end": v(-18.88, -5.79) * mm});
            skLineSegment(sketch, "E334", {"start": v(-18.88, -5.79) * mm, "end": v(-18.48, -5.9) * mm});
            skLineSegment(sketch, "E335", {"start": v(-18.48, -5.9) * mm, "end": v(-18.1, -5.97) * mm});
            skLineSegment(sketch, "E336", {"start": v(-18.1, -5.97) * mm, "end": v(-17.7, -6.02) * mm});
            skLineSegment(sketch, "E337", {"start": v(-17.7, -6.02) * mm, "end": v(-17.3, -6.04) * mm});
            skLineSegment(sketch, "E338", {"start": v(-17.3, -6.04) * mm, "end": v(-16.9, -6.04) * mm});
            skLineSegment(sketch, "E339", {"start": v(-16.9, -6.04) * mm, "end": v(-16.5, -6.01) * mm});
            skLineSegment(sketch, "E340", {"start": v(-16.5, -6.01) * mm, "end": v(-16.1, -5.95) * mm});
            skLineSegment(sketch, "E341", {"start": v(-16.1, -5.95) * mm, "end": v(-15.72, -5.87) * mm});
            skLineSegment(sketch, "E342", {"start": v(-15.72, -5.87) * mm, "end": v(-15.36, -5.7) * mm});
            skLineSegment(sketch, "E343", {"start": v(-15.36, -5.7) * mm, "end": v(-14.99, -5.54) * mm});
            skLineSegment(sketch, "E344", {"start": v(-14.99, -5.54) * mm, "end": v(-14.62, -5.37) * mm});
            skLineSegment(sketch, "E345", {"start": v(-14.62, -5.37) * mm, "end": v(-14.26, -5.2) * mm});
            skLineSegment(sketch, "E346", {"start": v(-14.26, -5.2) * mm, "end": v(-13.89, -5.04) * mm});
            skLineSegment(sketch, "E347", {"start": v(-13.89, -5.04) * mm, "end": v(-13.52, -4.87) * mm});
            skLineSegment(sketch, "E348", {"start": v(-13.52, -4.87) * mm, "end": v(-13.15, -4.7) * mm});
            skLineSegment(sketch, "E349", {"start": v(-13.15, -4.7) * mm, "end": v(-12.79, -4.53) * mm});
            skLineSegment(sketch, "E350", {"start": v(-12.79, -4.53) * mm, "end": v(-12.42, -4.36) * mm});
            skLineSegment(sketch, "E351", {"start": v(-12.42, -4.36) * mm, "end": v(-12.05, -4.2) * mm});
            skLineSegment(sketch, "E352", {"start": v(-12.05, -4.2) * mm, "end": v(-11.83, -4.54) * mm});
            skLineSegment(sketch, "E353", {"start": v(-11.83, -4.54) * mm, "end": v(-11.6, -4.89) * mm});
            skLineSegment(sketch, "E354", {"start": v(-11.6, -4.89) * mm, "end": v(-11.38, -5.23) * mm});
            skLineSegment(sketch, "E355", {"start": v(-11.38, -5.23) * mm, "end": v(-11.16, -5.58) * mm});
            skLineSegment(sketch, "E356", {"start": v(-11.16, -5.58) * mm, "end": v(-10.94, -5.92) * mm});
            skLineSegment(sketch, "E357", {"start": v(-10.94, -5.92) * mm, "end": v(-10.72, -6.27) * mm});
            skLineSegment(sketch, "E358", {"start": v(-10.72, -6.27) * mm, "end": v(-10.5, -6.62) * mm});
            skLineSegment(sketch, "E359", {"start": v(-10.5, -6.62) * mm, "end": v(-10.8, -6.88) * mm});
            skLineSegment(sketch, "E360", {"start": v(-10.8, -6.88) * mm, "end": v(-11.1, -7.15) * mm});
            skLineSegment(sketch, "E361", {"start": v(-11.1, -7.15) * mm, "end": v(-11.41, -7.4) * mm});
            skLineSegment(sketch, "E362", {"start": v(-11.41, -7.4) * mm, "end": v(-11.72, -7.67) * mm});
            skLineSegment(sketch, "E363", {"start": v(-11.72, -7.67) * mm, "end": v(-12.02, -7.94) * mm});
            skLineSegment(sketch, "E364", {"start": v(-12.02, -7.94) * mm, "end": v(-12.33, -8.2) * mm});
            skLineSegment(sketch, "E365", {"start": v(-12.33, -8.2) * mm, "end": v(-12.63, -8.47) * mm});
            skLineSegment(sketch, "E366", {"start": v(-12.63, -8.47) * mm, "end": v(-12.94, -8.73) * mm});
            skLineSegment(sketch, "E367", {"start": v(-12.94, -8.73) * mm, "end": v(-13.24, -9) * mm});
            skLineSegment(sketch, "E368", {"start": v(-13.24, -9) * mm, "end": v(-13.55, -9.26) * mm});
            skLineSegment(sketch, "E369", {"start": v(-13.55, -9.26) * mm, "end": v(-13.79, -9.6) * mm});
            skLineSegment(sketch, "E370", {"start": v(-13.79, -9.6) * mm, "end": v(-14, -9.92) * mm});
            skLineSegment(sketch, "E371", {"start": v(-14, -9.92) * mm, "end": v(-14.2, -10.28) * mm});
            skLineSegment(sketch, "E372", {"start": v(-14.2, -10.28) * mm, "end": v(-14.36, -10.63) * mm});
            skLineSegment(sketch, "E373", {"start": v(-14.36, -10.63) * mm, "end": v(-14.5, -11.01) * mm});
            skLineSegment(sketch, "E374", {"start": v(-14.5, -11.01) * mm, "end": v(-14.62, -11.38) * mm});
            skLineSegment(sketch, "E375", {"start": v(-14.62, -11.38) * mm, "end": v(-14.71, -11.78) * mm});
            skLineSegment(sketch, "E376", {"start": v(-14.71, -11.78) * mm, "end": v(-14.78, -12.16) * mm});
            skLineSegment(sketch, "E377", {"start": v(-14.78, -12.16) * mm, "end": v(-14.82, -12.57) * mm});
            skLineSegment(sketch, "E378", {"start": v(-14.82, -12.57) * mm, "end": v(-14.83, -12.96) * mm});
            skLineSegment(sketch, "E379", {"start": v(-14.83, -12.96) * mm, "end": v(-14.81, -13.37) * mm});
            skLineSegment(sketch, "E380", {"start": v(-14.81, -13.37) * mm, "end": v(-14.78, -13.75) * mm});
            skLineSegment(sketch, "E381", {"start": v(-14.78, -13.75) * mm, "end": v(-14.37, -13.73) * mm});
            skLineSegment(sketch, "E382", {"start": v(-14.37, -13.73) * mm, "end": v(-13.98, -13.7) * mm});
            skLineSegment(sketch, "E383", {"start": v(-13.98, -13.7) * mm, "end": v(-13.58, -13.62) * mm});
            skLineSegment(sketch, "E384", {"start": v(-13.58, -13.62) * mm, "end": v(-13.2, -13.53) * mm});
            skLineSegment(sketch, "E385", {"start": v(-13.2, -13.53) * mm, "end": v(-12.81, -13.4) * mm});
            skLineSegment(sketch, "E386", {"start": v(-12.81, -13.4) * mm, "end": v(-12.45, -13.26) * mm});
            skLineSegment(sketch, "E387", {"start": v(-12.45, -13.26) * mm, "end": v(-12.08, -13.08) * mm});
            skLineSegment(sketch, "E388", {"start": v(-12.08, -13.08) * mm, "end": v(-11.75, -12.9) * mm});
            skLineSegment(sketch, "E389", {"start": v(-11.75, -12.9) * mm, "end": v(-11.4, -12.67) * mm});
            skLineSegment(sketch, "E390", {"start": v(-11.4, -12.67) * mm, "end": v(-11.1, -12.44) * mm});
            skLineSegment(sketch, "E391", {"start": v(-11.1, -12.44) * mm, "end": v(-10.78, -12.17) * mm});
            skLineSegment(sketch, "E392", {"start": v(-10.78, -12.17) * mm, "end": v(-10.5, -11.9) * mm});
            skLineSegment(sketch, "E393", {"start": v(-10.5, -11.9) * mm, "end": v(-10.29, -11.56) * mm});
            skLineSegment(sketch, "E394", {"start": v(-10.29, -11.56) * mm, "end": v(-10.07, -11.22) * mm});
            skLineSegment(sketch, "E395", {"start": v(-10.07, -11.22) * mm, "end": v(-9.85, -10.88) * mm});
            skLineSegment(sketch, "E396", {"start": v(-9.85, -10.88) * mm, "end": v(-9.63, -10.54) * mm});
            skLineSegment(sketch, "E397", {"start": v(-9.63, -10.54) * mm, "end": v(-9.41, -10.2) * mm});
            skLineSegment(sketch, "E398", {"start": v(-9.41, -10.2) * mm, "end": v(-9.2, -9.86) * mm});
            skLineSegment(sketch, "E399", {"start": v(-9.2, -9.86) * mm, "end": v(-8.98, -9.52) * mm});
            skLineSegment(sketch, "E400", {"start": v(-8.98, -9.52) * mm, "end": v(-8.76, -9.18) * mm});
            skLineSegment(sketch, "E401", {"start": v(-8.76, -9.18) * mm, "end": v(-8.54, -8.84) * mm});
            skLineSegment(sketch, "E402", {"start": v(-8.54, -8.84) * mm, "end": v(-8.32, -8.5) * mm});
            skLineSegment(sketch, "E403", {"start": v(-8.32, -8.5) * mm, "end": v(-7.95, -8.67) * mm});
            skLineSegment(sketch, "E404", {"start": v(-7.95, -8.67) * mm, "end": v(-7.58, -8.84) * mm});
            skLineSegment(sketch, "E405", {"start": v(-7.58, -8.84) * mm, "end": v(-7.2, -9.01) * mm});
            skLineSegment(sketch, "E406", {"start": v(-7.2, -9.01) * mm, "end": v(-6.83, -9.18) * mm});
            skLineSegment(sketch, "E407", {"start": v(-6.83, -9.18) * mm, "end": v(-6.46, -9.35) * mm});
            skLineSegment(sketch, "E408", {"start": v(-6.46, -9.35) * mm, "end": v(-6.08, -9.52) * mm});
            skLineSegment(sketch, "E409", {"start": v(-6.08, -9.52) * mm, "end": v(-5.7, -9.7) * mm});
            skLineSegment(sketch, "E410", {"start": v(-5.7, -9.7) * mm, "end": v(-5.82, -10.08) * mm});
            skLineSegment(sketch, "E411", {"start": v(-5.82, -10.08) * mm, "end": v(-5.93, -10.47) * mm});
            skLineSegment(sketch, "E412", {"start": v(-5.93, -10.47) * mm, "end": v(-6.05, -10.86) * mm});
            skLineSegment(sketch, "E413", {"start": v(-6.05, -10.86) * mm, "end": v(-6.16, -11.24) * mm});
            skLineSegment(sketch, "E414", {"start": v(-6.16, -11.24) * mm, "end": v(-6.28, -11.63) * mm});
            skLineSegment(sketch, "E415", {"start": v(-6.28, -11.63) * mm, "end": v(-6.39, -12.02) * mm});
            skLineSegment(sketch, "E416", {"start": v(-6.39, -12.02) * mm, "end": v(-6.5, -12.4) * mm});
            skLineSegment(sketch, "E417", {"start": v(-6.5, -12.4) * mm, "end": v(-6.62, -12.8) * mm});
            skLineSegment(sketch, "E418", {"start": v(-6.62, -12.8) * mm, "end": v(-6.73, -13.18) * mm});
            skLineSegment(sketch, "E419", {"start": v(-6.73, -13.18) * mm, "end": v(-6.84, -13.57) * mm});
            skLineSegment(sketch, "E420", {"start": v(-6.84, -13.57) * mm, "end": v(-6.87, -13.98) * mm});
            skLineSegment(sketch, "E421", {"start": v(-6.87, -13.98) * mm, "end": v(-6.87, -14.37) * mm});
            skLineSegment(sketch, "E422", {"start": v(-6.87, -14.37) * mm, "end": v(-6.84, -14.78) * mm});
            skLineSegment(sketch, "E423", {"start": v(-6.84, -14.78) * mm, "end": v(-6.79, -15.16) * mm});
            skLineSegment(sketch, "E424", {"start": v(-6.79, -15.16) * mm, "end": v(-6.7, -15.56) * mm});
            skLineSegment(sketch, "E425", {"start": v(-6.7, -15.56) * mm, "end": v(-6.6, -15.93) * mm});
            skLineSegment(sketch, "E426", {"start": v(-6.6, -15.93) * mm, "end": v(-6.46, -16.32) * mm});
            skLineSegment(sketch, "E427", {"start": v(-6.46, -16.32) * mm, "end": v(-6.3, -16.68) * mm});
            skLineSegment(sketch, "E428", {"start": v(-6.3, -16.68) * mm, "end": v(-6.12, -17.04) * mm});
            skLineSegment(sketch, "E429", {"start": v(-6.12, -17.04) * mm, "end": v(-5.92, -17.37) * mm});
            skLineSegment(sketch, "E430", {"start": v(-5.92, -17.37) * mm, "end": v(-5.69, -17.7) * mm});
            skLineSegment(sketch, "E431", {"start": v(-5.69, -17.7) * mm, "end": v(-5.45, -18.01) * mm});
            skLineSegment(sketch, "E432", {"start": v(-5.45, -18.01) * mm, "end": v(-5.12, -17.78) * mm});
            skLineSegment(sketch, "E433", {"start": v(-5.12, -17.78) * mm, "end": v(-4.82, -17.53) * mm});
            skLineSegment(sketch, "E434", {"start": v(-4.82, -17.53) * mm, "end": v(-4.52, -17.25) * mm});
            skLineSegment(sketch, "E435", {"start": v(-4.52, -17.25) * mm, "end": v(-4.25, -16.97) * mm});
            skLineSegment(sketch, "E436", {"start": v(-4.25, -16.97) * mm, "end": v(-4, -16.65) * mm});
            skLineSegment(sketch, "E437", {"start": v(-4, -16.65) * mm, "end": v(-3.76, -16.34) * mm});
            skLineSegment(sketch, "E438", {"start": v(-3.76, -16.34) * mm, "end": v(-3.55, -16) * mm});
            skLineSegment(sketch, "E439", {"start": v(-3.55, -16) * mm, "end": v(-3.36, -15.65) * mm});
            skLineSegment(sketch, "E440", {"start": v(-3.36, -15.65) * mm, "end": v(-3.2, -15.27) * mm});
            skLineSegment(sketch, "E441", {"start": v(-3.2, -15.27) * mm, "end": v(-3.06, -14.91) * mm});
            skLineSegment(sketch, "E442", {"start": v(-3.06, -14.91) * mm, "end": v(-2.95, -14.52) * mm});
            skLineSegment(sketch, "E443", {"start": v(-2.95, -14.52) * mm, "end": v(-2.86, -14.14) * mm});
            skLineSegment(sketch, "E444", {"start": v(-2.86, -14.14) * mm, "end": v(-2.86, -13.74) * mm});
            skLineSegment(sketch, "E445", {"start": v(-2.86, -13.74) * mm, "end": v(-2.86, -13.33) * mm});
            skLineSegment(sketch, "E446", {"start": v(-2.86, -13.33) * mm, "end": v(-2.86, -12.93) * mm});
            skLineSegment(sketch, "E447", {"start": v(-2.86, -12.93) * mm, "end": v(-2.86, -12.53) * mm});
            skLineSegment(sketch, "E448", {"start": v(-2.86, -12.53) * mm, "end": v(-2.86, -12.12) * mm});
            skLineSegment(sketch, "E449", {"start": v(-2.86, -12.12) * mm, "end": v(-2.86, -11.72) * mm});
            skLineSegment(sketch, "E450", {"start": v(-2.86, -11.72) * mm, "end": v(-2.86, -11.31) * mm});
            skLineSegment(sketch, "E451", {"start": v(-2.86, -11.31) * mm, "end": v(-2.86, -10.91) * mm});
            skLineSegment(sketch, "E452", {"start": v(-2.86, -10.91) * mm, "end": v(-2.86, -10.5) * mm});
            skLineSegment(sketch, "E453", {"start": v(-2.86, -10.5) * mm, "end": v(-2.86, -10.1) * mm});
            skLineSegment(sketch, "E454", {"start": v(-2.86, -10.1) * mm, "end": v(-2.45, -10.04) * mm});
            skLineSegment(sketch, "E455", {"start": v(-2.45, -10.04) * mm, "end": v(-2.05, -9.99) * mm});
            skLineSegment(sketch, "E456", {"start": v(-2.05, -9.99) * mm, "end": v(-1.64, -9.93) * mm});
            skLineSegment(sketch, "E457", {"start": v(-1.64, -9.93) * mm, "end": v(-1.24, -9.87) * mm});
            skLineSegment(sketch, "E458", {"start": v(-1.24, -9.87) * mm, "end": v(-0.83, -9.81) * mm});
            skLineSegment(sketch, "E459", {"start": v(-0.83, -9.81) * mm, "end": v(-0.42, -9.75) * mm});
            skLineSegment(sketch, "E460", {"start": v(-0.42, -9.75) * mm, "end": v(-0.01, -9.7) * mm});
            skLineSegment(sketch, "E461", {"start": v(-0.01, -9.7) * mm, "end": v(0.1, -10.08) * mm});
            skLineSegment(sketch, "E462", {"start": v(0.1, -10.08) * mm, "end": v(0.21, -10.47) * mm});
            skLineSegment(sketch, "E463", {"start": v(0.21, -10.47) * mm, "end": v(0.33, -10.86) * mm});
            skLineSegment(sketch, "E464", {"start": v(0.33, -10.86) * mm, "end": v(0.44, -11.24) * mm});
            skLineSegment(sketch, "E465", {"start": v(0.44, -11.24) * mm, "end": v(0.55, -11.63) * mm});
            skLineSegment(sketch, "E466", {"start": v(0.55, -11.63) * mm, "end": v(0.67, -12.02) * mm});
            skLineSegment(sketch, "E467", {"start": v(0.67, -12.02) * mm, "end": v(0.78, -12.4) * mm});
            skLineSegment(sketch, "E468", {"start": v(0.78, -12.4) * mm, "end": v(0.9, -12.8) * mm});
            skLineSegment(sketch, "E469", {"start": v(0.9, -12.8) * mm, "end": v(1.01, -13.18) * mm});
            skLineSegment(sketch, "E470", {"start": v(1.01, -13.18) * mm, "end": v(1.12, -13.57) * mm});
            skLineSegment(sketch, "E471", {"start": v(1.12, -13.57) * mm, "end": v(1.33, -13.93) * mm});
            skLineSegment(sketch, "E472", {"start": v(1.33, -13.93) * mm, "end": v(1.53, -14.25) * mm});
            skLineSegment(sketch, "E473", {"start": v(1.53, -14.25) * mm, "end": v(1.78, -14.58) * mm});
            skLineSegment(sketch, "E474", {"start": v(1.78, -14.58) * mm, "end": v(2.03, -14.87) * mm});
            skLineSegment(sketch, "E475", {"start": v(2.03, -14.87) * mm, "end": v(2.32, -15.17) * mm});
            skLineSegment(sketch, "E476", {"start": v(2.32, -15.17) * mm, "end": v(2.6, -15.42) * mm});
            skLineSegment(sketch, "E477", {"start": v(2.6, -15.42) * mm, "end": v(2.93, -15.67) * mm});
            skLineSegment(sketch, "E478", {"start": v(2.93, -15.67) * mm, "end": v(3.25, -15.9) * mm});
            skLineSegment(sketch, "E479", {"start": v(3.25, -15.9) * mm, "end": v(3.6, -16.1) * mm});
            skLineSegment(sketch, "E480", {"start": v(3.6, -16.1) * mm, "end": v(3.95, -16.27) * mm});
            skLineSegment(sketch, "E481", {"start": v(3.95, -16.27) * mm, "end": v(4.33, -16.43) * mm});
            skLineSegment(sketch, "E482", {"start": v(4.33, -16.43) * mm, "end": v(4.7, -16.55) * mm});
            skLineSegment(sketch, "E483", {"start": v(4.7, -16.55) * mm, "end": v(4.85, -16.17) * mm});
            skLineSegment(sketch, "E484", {"start": v(4.85, -16.17) * mm, "end": v(4.97, -15.8) * mm});
            skLineSegment(sketch, "E485", {"start": v(4.97, -15.8) * mm, "end": v(5.07, -15.4) * mm});
            skLineSegment(sketch, "E486", {"start": v(5.07, -15.4) * mm, "end": v(5.15, -15.03) * mm});
            skLineSegment(sketch, "E487", {"start": v(5.15, -15.03) * mm, "end": v(5.2, -14.62) * mm});
            skLineSegment(sketch, "E488", {"start": v(5.2, -14.62) * mm, "end": v(5.21, -14.23) * mm});
            skLineSegment(sketch, "E489", {"start": v(5.21, -14.23) * mm, "end": v(5.2, -13.82) * mm});
            skLineSegment(sketch, "E490", {"start": v(5.2, -13.82) * mm, "end": v(5.18, -13.44) * mm});
            skLineSegment(sketch, "E491", {"start": v(5.18, -13.44) * mm, "end": v(5.11, -13.03) * mm});
            skLineSegment(sketch, "E492", {"start": v(5.11, -13.03) * mm, "end": v(5.03, -12.65) * mm});
            skLineSegment(sketch, "E493", {"start": v(5.03, -12.65) * mm, "end": v(4.92, -12.26) * mm});
            skLineSegment(sketch, "E494", {"start": v(4.92, -12.26) * mm, "end": v(4.79, -11.9) * mm});
            skLineSegment(sketch, "E495", {"start": v(4.79, -11.9) * mm, "end": v(4.57, -11.56) * mm});
            skLineSegment(sketch, "E496", {"start": v(4.57, -11.56) * mm, "end": v(4.35, -11.22) * mm});
            skLineSegment(sketch, "E497", {"start": v(4.35, -11.22) * mm, "end": v(4.13, -10.88) * mm});
            skLineSegment(sketch, "E498", {"start": v(4.13, -10.88) * mm, "end": v(3.91, -10.54) * mm});
            skLineSegment(sketch, "E499", {"start": v(3.91, -10.54) * mm, "end": v(3.7, -10.2) * mm});
            skLineSegment(sketch, "E500", {"start": v(3.7, -10.2) * mm, "end": v(3.48, -9.86) * mm});
            skLineSegment(sketch, "E501", {"start": v(3.48, -9.86) * mm, "end": v(3.26, -9.52) * mm});
            skLineSegment(sketch, "E502", {"start": v(3.26, -9.52) * mm, "end": v(3.04, -9.18) * mm});
            skLineSegment(sketch, "E503", {"start": v(3.04, -9.18) * mm, "end": v(2.82, -8.84) * mm});
            skLineSegment(sketch, "E504", {"start": v(2.82, -8.84) * mm, "end": v(2.6, -8.5) * mm});
            skLineSegment(sketch, "E505", {"start": v(2.6, -8.5) * mm, "end": v(2.91, -8.23) * mm});
            skLineSegment(sketch, "E506", {"start": v(2.91, -8.23) * mm, "end": v(3.22, -7.96) * mm});
            skLineSegment(sketch, "E507", {"start": v(3.22, -7.96) * mm, "end": v(3.53, -7.7) * mm});
            skLineSegment(sketch, "E508", {"start": v(3.53, -7.7) * mm, "end": v(3.84, -7.42) * mm});
            skLineSegment(sketch, "E509", {"start": v(3.84, -7.42) * mm, "end": v(4.15, -7.16) * mm});
            skLineSegment(sketch, "E510", {"start": v(4.15, -7.16) * mm, "end": v(4.46, -6.89) * mm});
            skLineSegment(sketch, "E511", {"start": v(4.46, -6.89) * mm, "end": v(4.77, -6.62) * mm});
            skLineSegment(sketch, "E512", {"start": v(4.77, -6.62) * mm, "end": v(5.08, -6.88) * mm});
            skLineSegment(sketch, "E513", {"start": v(5.08, -6.88) * mm, "end": v(5.39, -7.15) * mm});
            skLineSegment(sketch, "E514", {"start": v(5.39, -7.15) * mm, "end": v(5.7, -7.4) * mm});
            skLineSegment(sketch, "E515", {"start": v(5.7, -7.4) * mm, "end": v(6, -7.67) * mm});
            skLineSegment(sketch, "E516", {"start": v(6, -7.67) * mm, "end": v(6.3, -7.94) * mm});
            skLineSegment(sketch, "E517", {"start": v(6.3, -7.94) * mm, "end": v(6.6, -8.2) * mm});
            skLineSegment(sketch, "E518", {"start": v(6.6, -8.2) * mm, "end": v(6.91, -8.47) * mm});
            skLineSegment(sketch, "E519", {"start": v(6.91, -8.47) * mm, "end": v(7.22, -8.73) * mm});
            skLineSegment(sketch, "E520", {"start": v(7.22, -8.73) * mm, "end": v(7.52, -9) * mm});
            skLineSegment(sketch, "E521", {"start": v(7.52, -9) * mm, "end": v(7.83, -9.26) * mm});
            skLineSegment(sketch, "E522", {"start": v(7.83, -9.26) * mm, "end": v(8.2, -9.45) * mm});
            skLineSegment(sketch, "E523", {"start": v(8.2, -9.45) * mm, "end": v(8.54, -9.61) * mm});
            skLineSegment(sketch, "E524", {"start": v(8.54, -9.61) * mm, "end": v(8.93, -9.75) * mm});
            skLineSegment(sketch, "E525", {"start": v(8.93, -9.75) * mm, "end": v(9.3, -9.87) * mm});
            skLineSegment(sketch, "E526", {"start": v(9.3, -9.87) * mm, "end": v(9.7, -9.96) * mm});
            skLineSegment(sketch, "E527", {"start": v(9.7, -9.96) * mm, "end": v(10.08, -10.02) * mm});
            skLineSegment(sketch, "E528", {"start": v(10.08, -10.02) * mm, "end": v(10.49, -10.05) * mm});
            skLineSegment(sketch, "E529", {"start": v(10.49, -10.05) * mm, "end": v(10.88, -10.06) * mm});
            skLineSegment(sketch, "E530", {"start": v(10.88, -10.06) * mm, "end": v(11.29, -10.04) * mm});
            skLineSegment(sketch, "E531", {"start": v(11.29, -10.04) * mm, "end": v(11.67, -10) * mm});
            skLineSegment(sketch, "E532", {"start": v(11.67, -10) * mm, "end": v(12.07, -9.93) * mm});
            skLineSegment(sketch, "E533", {"start": v(12.07, -9.93) * mm, "end": v(12.45, -9.84) * mm});
            skLineSegment(sketch, "E534", {"start": v(12.45, -9.84) * mm, "end": v(12.37, -9.44) * mm});
            skLineSegment(sketch, "E535", {"start": v(12.37, -9.44) * mm, "end": v(12.28, -9.06) * mm});
            skLineSegment(sketch, "E536", {"start": v(12.28, -9.06) * mm, "end": v(12.14, -8.67) * mm});
            skLineSegment(sketch, "E537", {"start": v(12.14, -8.67) * mm, "end": v(12, -8.31) * mm});
            skLineSegment(sketch, "E538", {"start": v(12, -8.31) * mm, "end": v(11.82, -7.95) * mm});
            skLineSegment(sketch, "E539", {"start": v(11.82, -7.95) * mm, "end": v(11.63, -7.6) * mm});
            skLineSegment(sketch, "E540", {"start": v(11.63, -7.6) * mm, "end": v(11.4, -7.27) * mm});
            skLineSegment(sketch, "E541", {"start": v(11.4, -7.27) * mm, "end": v(11.17, -6.96) * mm});
            skLineSegment(sketch, "E542", {"start": v(11.17, -6.96) * mm, "end": v(10.9, -6.65) * mm});
            skLineSegment(sketch, "E543", {"start": v(10.9, -6.65) * mm, "end": v(10.62, -6.38) * mm});
            skLineSegment(sketch, "E544", {"start": v(10.62, -6.38) * mm, "end": v(10.31, -6.11) * mm});
            skLineSegment(sketch, "E545", {"start": v(10.31, -6.11) * mm, "end": v(10, -5.87) * mm});
            skLineSegment(sketch, "E546", {"start": v(10, -5.87) * mm, "end": v(9.64, -5.7) * mm});
            skLineSegment(sketch, "E547", {"start": v(9.64, -5.7) * mm, "end": v(9.27, -5.54) * mm});
            skLineSegment(sketch, "E548", {"start": v(9.27, -5.54) * mm, "end": v(8.9, -5.37) * mm});
            skLineSegment(sketch, "E549", {"start": v(8.9, -5.37) * mm, "end": v(8.53, -5.2) * mm});
            skLineSegment(sketch, "E550", {"start": v(8.53, -5.2) * mm, "end": v(8.17, -5.04) * mm});
            skLineSegment(sketch, "E551", {"start": v(8.17, -5.04) * mm, "end": v(7.8, -4.87) * mm});
            skLineSegment(sketch, "E552", {"start": v(7.8, -4.87) * mm, "end": v(7.43, -4.7) * mm});
            skLineSegment(sketch, "E553", {"start": v(7.43, -4.7) * mm, "end": v(7.06, -4.53) * mm});
            skLineSegment(sketch, "E554", {"start": v(7.06, -4.53) * mm, "end": v(6.7, -4.36) * mm});
            skLineSegment(sketch, "E555", {"start": v(6.7, -4.36) * mm, "end": v(6.33, -4.2) * mm});
            skLineSegment(sketch, "E556", {"start": v(6.33, -4.2) * mm, "end": v(6.45, -3.8) * mm});
            skLineSegment(sketch, "E557", {"start": v(6.45, -3.8) * mm, "end": v(6.56, -3.4) * mm});
            skLineSegment(sketch, "E558", {"start": v(6.56, -3.4) * mm, "end": v(6.68, -3.02) * mm});
            skLineSegment(sketch, "E559", {"start": v(6.68, -3.02) * mm, "end": v(6.8, -2.62) * mm});
            skLineSegment(sketch, "E560", {"start": v(6.8, -2.62) * mm, "end": v(6.9, -2.23) * mm});
            skLineSegment(sketch, "E561", {"start": v(6.9, -2.23) * mm, "end": v(7.02, -1.83) * mm});
            skLineSegment(sketch, "E562", {"start": v(7.02, -1.83) * mm, "end": v(7.14, -1.44) * mm});
            skCircle(sketch, "E563", {"center": v(-2.86, 0) * mm, "radius": 3 * mm});
            skSolve(sketch);
        }
        {
            var Q0;
            Q0=makeQuery(id+"F0.imprint","IMPRINT",FACE,{"disambiguationData":[TD([[makeQuery(id+"F0.imprint","IMPRINT",EDGE,{"derivedFrom":sQuery(id+"F0.wireOp",EDGE,"E0")}),1.0]])]});
            extrude(context, id + "F1", {"entities" : qUnion([Q0]), "depth" : 8 * mm});
        }
        {
            var Q0;
            Q0=makeQuery(id+"F1.opExtrude","CAP_FACE",FACE,{"disambiguationData":[OSD([sQuery(id+"F0.wireOp",EDGE,"E0"),sQuery(id+"F0.wireOp",EDGE,"E1"),sQuery(id+"F0.wireOp",EDGE,"E2"),sQuery(id+"F0.wireOp",EDGE,"E3"),sQuery(id+"F0.wireOp",EDGE,"E4"),sQuery(id+"F0.wireOp",EDGE,"E5"),sQuery(id+"F0.wireOp",EDGE,"E6"),sQuery(id+"F0.wireOp",EDGE,"E7"),sQuery(id+"F0.wireOp",EDGE,"E8"),sQuery(id+"F0.wireOp",EDGE,"E9"),sQuery(id+"F0.wireOp",EDGE,"E10"),sQuery(id+"F0.wireOp",EDGE,"E11"),sQuery(id+"F0.wireOp",EDGE,"E12"),sQuery(id+"F0.wireOp",EDGE,"E13"),sQuery(id+"F0.wireOp",EDGE,"E14"),sQuery(id+"F0.wireOp",EDGE,"E15"),sQuery(id+"F0.wireOp",EDGE,"E16"),sQuery(id+"F0.wireOp",EDGE,"E17"),sQuery(id+"F0.wireOp",EDGE,"E18"),sQuery(id+"F0.wireOp",EDGE,"E19"),sQuery(id+"F0.wireOp",EDGE,"E20"),sQuery(id+"F0.wireOp",EDGE,"E21"),sQuery(id+"F0.wireOp",EDGE,"E22"),sQuery(id+"F0.wireOp",EDGE,"E23"),sQuery(id+"F0.wireOp",EDGE,"E24"),sQuery(id+"F0.wireOp",EDGE,"E25"),sQuery(id+"F0.wireOp",EDGE,"E26"),sQuery(id+"F0.wireOp",EDGE,"E27"),sQuery(id+"F0.wireOp",EDGE,"E28"),sQuery(id+"F0.wireOp",EDGE,"E29"),sQuery(id+"F0.wireOp",EDGE,"E30"),sQuery(id+"F0.wireOp",EDGE,"E31"),sQuery(id+"F0.wireOp",EDGE,"E32"),sQuery(id+"F0.wireOp",EDGE,"E33"),sQuery(id+"F0.wireOp",EDGE,"E34"),sQuery(id+"F0.wireOp",EDGE,"E35"),sQuery(id+"F0.wireOp",EDGE,"E36"),sQuery(id+"F0.wireOp",EDGE,"E37"),sQuery(id+"F0.wireOp",EDGE,"E38"),sQuery(id+"F0.wireOp",EDGE,"E39"),sQuery(id+"F0.wireOp",EDGE,"E40"),sQuery(id+"F0.wireOp",EDGE,"E41"),sQuery(id+"F0.wireOp",EDGE,"E42"),sQuery(id+"F0.wireOp",EDGE,"E43"),sQuery(id+"F0.wireOp",EDGE,"E44"),sQuery(id+"F0.wireOp",EDGE,"E45"),sQuery(id+"F0.wireOp",EDGE,"E46"),sQuery(id+"F0.wireOp",EDGE,"E47"),sQuery(id+"F0.wireOp",EDGE,"E48"),sQuery(id+"F0.wireOp",EDGE,"E49"),sQuery(id+"F0.wireOp",EDGE,"E50"),sQuery(id+"F0.wireOp",EDGE,"E51"),sQuery(id+"F0.wireOp",EDGE,"E52"),sQuery(id+"F0.wireOp",EDGE,"E53"),sQuery(id+"F0.wireOp",EDGE,"E54"),sQuery(id+"F0.wireOp",EDGE,"E55"),sQuery(id+"F0.wireOp",EDGE,"E56"),sQuery(id+"F0.wireOp",EDGE,"E57"),sQuery(id+"F0.wireOp",EDGE,"E58"),sQuery(id+"F0.wireOp",EDGE,"E59"),sQuery(id+"F0.wireOp",EDGE,"E60"),sQuery(id+"F0.wireOp",EDGE,"E61"),sQuery(id+"F0.wireOp",EDGE,"E62"),sQuery(id+"F0.wireOp",EDGE,"E63"),sQuery(id+"F0.wireOp",EDGE,"E64"),sQuery(id+"F0.wireOp",EDGE,"E65"),sQuery(id+"F0.wireOp",EDGE,"E66"),sQuery(id+"F0.wireOp",EDGE,"E67"),sQuery(id+"F0.wireOp",EDGE,"E68"),sQuery(id+"F0.wireOp",EDGE,"E69"),sQuery(id+"F0.wireOp",EDGE,"E70"),sQuery(id+"F0.wireOp",EDGE,"E71"),sQuery(id+"F0.wireOp",EDGE,"E72"),sQuery(id+"F0.wireOp",EDGE,"E73"),sQuery(id+"F0.wireOp",EDGE,"E74"),sQuery(id+"F0.wireOp",EDGE,"E75"),sQuery(id+"F0.wireOp",EDGE,"E76"),sQuery(id+"F0.wireOp",EDGE,"E77"),sQuery(id+"F0.wireOp",EDGE,"E78"),sQuery(id+"F0.wireOp",EDGE,"E79"),sQuery(id+"F0.wireOp",EDGE,"E80"),sQuery(id+"F0.wireOp",EDGE,"E81"),sQuery(id+"F0.wireOp",EDGE,"E82"),sQuery(id+"F0.wireOp",EDGE,"E83"),sQuery(id+"F0.wireOp",EDGE,"E84"),sQuery(id+"F0.wireOp",EDGE,"E85"),sQuery(id+"F0.wireOp",EDGE,"E86"),sQuery(id+"F0.wireOp",EDGE,"E87"),sQuery(id+"F0.wireOp",EDGE,"E88"),sQuery(id+"F0.wireOp",EDGE,"E89"),sQuery(id+"F0.wireOp",EDGE,"E90"),sQuery(id+"F0.wireOp",EDGE,"E91"),sQuery(id+"F0.wireOp",EDGE,"E92"),sQuery(id+"F0.wireOp",EDGE,"E93"),sQuery(id+"F0.wireOp",EDGE,"E94"),sQuery(id+"F0.wireOp",EDGE,"E95"),sQuery(id+"F0.wireOp",EDGE,"E96"),sQuery(id+"F0.wireOp",EDGE,"E97"),sQuery(id+"F0.wireOp",EDGE,"E98"),sQuery(id+"F0.wireOp",EDGE,"E99"),sQuery(id+"F0.wireOp",EDGE,"E100"),sQuery(id+"F0.wireOp",EDGE,"E101"),sQuery(id+"F0.wireOp",EDGE,"E102"),sQuery(id+"F0.wireOp",EDGE,"E103"),sQuery(id+"F0.wireOp",EDGE,"E104"),sQuery(id+"F0.wireOp",EDGE,"E105"),sQuery(id+"F0.wireOp",EDGE,"E106"),sQuery(id+"F0.wireOp",EDGE,"E107"),sQuery(id+"F0.wireOp",EDGE,"E108"),sQuery(id+"F0.wireOp",EDGE,"E109"),sQuery(id+"F0.wireOp",EDGE,"E110"),sQuery(id+"F0.wireOp",EDGE,"E111"),sQuery(id+"F0.wireOp",EDGE,"E112"),sQuery(id+"F0.wireOp",EDGE,"E113"),sQuery(id+"F0.wireOp",EDGE,"E114"),sQuery(id+"F0.wireOp",EDGE,"E115"),sQuery(id+"F0.wireOp",EDGE,"E116"),sQuery(id+"F0.wireOp",EDGE,"E117"),sQuery(id+"F0.wireOp",EDGE,"E118"),sQuery(id+"F0.wireOp",EDGE,"E119"),sQuery(id+"F0.wireOp",EDGE,"E120"),sQuery(id+"F0.wireOp",EDGE,"E121"),sQuery(id+"F0.wireOp",EDGE,"E122"),sQuery(id+"F0.wireOp",EDGE,"E123"),sQuery(id+"F0.wireOp",EDGE,"E124"),sQuery(id+"F0.wireOp",EDGE,"E125"),sQuery(id+"F0.wireOp",EDGE,"E126"),sQuery(id+"F0.wireOp",EDGE,"E127"),sQuery(id+"F0.wireOp",EDGE,"E128"),sQuery(id+"F0.wireOp",EDGE,"E129"),sQuery(id+"F0.wireOp",EDGE,"E130"),sQuery(id+"F0.wireOp",EDGE,"E131"),sQuery(id+"F0.wireOp",EDGE,"E132"),sQuery(id+"F0.wireOp",EDGE,"E133"),sQuery(id+"F0.wireOp",EDGE,"E134"),sQuery(id+"F0.wireOp",EDGE,"E135"),sQuery(id+"F0.wireOp",EDGE,"E136"),sQuery(id+"F0.wireOp",EDGE,"E137"),sQuery(id+"F0.wireOp",EDGE,"E138"),sQuery(id+"F0.wireOp",EDGE,"E139"),sQuery(id+"F0.wireOp",EDGE,"E140"),sQuery(id+"F0.wireOp",EDGE,"E141"),sQuery(id+"F0.wireOp",EDGE,"E142"),sQuery(id+"F0.wireOp",EDGE,"E143"),sQuery(id+"F0.wireOp",EDGE,"E144"),sQuery(id+"F0.wireOp",EDGE,"E145"),sQuery(id+"F0.wireOp",EDGE,"E146"),sQuery(id+"F0.wireOp",EDGE,"E147"),sQuery(id+"F0.wireOp",EDGE,"E148"),sQuery(id+"F0.wireOp",EDGE,"E149"),sQuery(id+"F0.wireOp",EDGE,"E150"),sQuery(id+"F0.wireOp",EDGE,"E151"),sQuery(id+"F0.wireOp",EDGE,"E152"),sQuery(id+"F0.wireOp",EDGE,"E153"),sQuery(id+"F0.wireOp",EDGE,"E154"),sQuery(id+"F0.wireOp",EDGE,"E155"),sQuery(id+"F0.wireOp",EDGE,"E156"),sQuery(id+"F0.wireOp",EDGE,"E157"),sQuery(id+"F0.wireOp",EDGE,"E158"),sQuery(id+"F0.wireOp",EDGE,"E159"),sQuery(id+"F0.wireOp",EDGE,"E160"),sQuery(id+"F0.wireOp",EDGE,"E161"),sQuery(id+"F0.wireOp",EDGE,"E162"),sQuery(id+"F0.wireOp",EDGE,"E163"),sQuery(id+"F0.wireOp",EDGE,"E164"),sQuery(id+"F0.wireOp",EDGE,"E165"),sQuery(id+"F0.wireOp",EDGE,"E166"),sQuery(id+"F0.wireOp",EDGE,"E167"),sQuery(id+"F0.wireOp",EDGE,"E168"),sQuery(id+"F0.wireOp",EDGE,"E169"),sQuery(id+"F0.wireOp",EDGE,"E170"),sQuery(id+"F0.wireOp",EDGE,"E171"),sQuery(id+"F0.wireOp",EDGE,"E172"),sQuery(id+"F0.wireOp",EDGE,"E173"),sQuery(id+"F0.wireOp",EDGE,"E174"),sQuery(id+"F0.wireOp",EDGE,"E175"),sQuery(id+"F0.wireOp",EDGE,"E176"),sQuery(id+"F0.wireOp",EDGE,"E177"),sQuery(id+"F0.wireOp",EDGE,"E178"),sQuery(id+"F0.wireOp",EDGE,"E179"),sQuery(id+"F0.wireOp",EDGE,"E180"),sQuery(id+"F0.wireOp",EDGE,"E181"),sQuery(id+"F0.wireOp",EDGE,"E182"),sQuery(id+"F0.wireOp",EDGE,"E183"),sQuery(id+"F0.wireOp",EDGE,"E184"),sQuery(id+"F0.wireOp",EDGE,"E185"),sQuery(id+"F0.wireOp",EDGE,"E186"),sQuery(id+"F0.wireOp",EDGE,"E187"),sQuery(id+"F0.wireOp",EDGE,"E188"),sQuery(id+"F0.wireOp",EDGE,"E189"),sQuery(id+"F0.wireOp",EDGE,"E190"),sQuery(id+"F0.wireOp",EDGE,"E191"),sQuery(id+"F0.wireOp",EDGE,"E192"),sQuery(id+"F0.wireOp",EDGE,"E193"),sQuery(id+"F0.wireOp",EDGE,"E194"),sQuery(id+"F0.wireOp",EDGE,"E195"),sQuery(id+"F0.wireOp",EDGE,"E196"),sQuery(id+"F0.wireOp",EDGE,"E197"),sQuery(id+"F0.wireOp",EDGE,"E198"),sQuery(id+"F0.wireOp",EDGE,"E199"),sQuery(id+"F0.wireOp",EDGE,"E200"),sQuery(id+"F0.wireOp",EDGE,"E201"),sQuery(id+"F0.wireOp",EDGE,"E202"),sQuery(id+"F0.wireOp",EDGE,"E203"),sQuery(id+"F0.wireOp",EDGE,"E204"),sQuery(id+"F0.wireOp",EDGE,"E205"),sQuery(id+"F0.wireOp",EDGE,"E206"),sQuery(id+"F0.wireOp",EDGE,"E207"),sQuery(id+"F0.wireOp",EDGE,"E208"),sQuery(id+"F0.wireOp",EDGE,"E209"),sQuery(id+"F0.wireOp",EDGE,"E210"),sQuery(id+"F0.wireOp",EDGE,"E211"),sQuery(id+"F0.wireOp",EDGE,"E212"),sQuery(id+"F0.wireOp",EDGE,"E213"),sQuery(id+"F0.wireOp",EDGE,"E214"),sQuery(id+"F0.wireOp",EDGE,"E215"),sQuery(id+"F0.wireOp",EDGE,"E216"),sQuery(id+"F0.wireOp",EDGE,"E217"),sQuery(id+"F0.wireOp",EDGE,"E218"),sQuery(id+"F0.wireOp",EDGE,"E219"),sQuery(id+"F0.wireOp",EDGE,"E220"),sQuery(id+"F0.wireOp",EDGE,"E221"),sQuery(id+"F0.wireOp",EDGE,"E222"),sQuery(id+"F0.wireOp",EDGE,"E223"),sQuery(id+"F0.wireOp",EDGE,"E224"),sQuery(id+"F0.wireOp",EDGE,"E225"),sQuery(id+"F0.wireOp",EDGE,"E226"),sQuery(id+"F0.wireOp",EDGE,"E227"),sQuery(id+"F0.wireOp",EDGE,"E228"),sQuery(id+"F0.wireOp",EDGE,"E229"),sQuery(id+"F0.wireOp",EDGE,"E230"),sQuery(id+"F0.wireOp",EDGE,"E231"),sQuery(id+"F0.wireOp",EDGE,"E232"),sQuery(id+"F0.wireOp",EDGE,"E233"),sQuery(id+"F0.wireOp",EDGE,"E234"),sQuery(id+"F0.wireOp",EDGE,"E235"),sQuery(id+"F0.wireOp",EDGE,"E236"),sQuery(id+"F0.wireOp",EDGE,"E237"),sQuery(id+"F0.wireOp",EDGE,"E238"),sQuery(id+"F0.wireOp",EDGE,"E239"),sQuery(id+"F0.wireOp",EDGE,"E240"),sQuery(id+"F0.wireOp",EDGE,"E241"),sQuery(id+"F0.wireOp",EDGE,"E242"),sQuery(id+"F0.wireOp",EDGE,"E243"),sQuery(id+"F0.wireOp",EDGE,"E244"),sQuery(id+"F0.wireOp",EDGE,"E245"),sQuery(id+"F0.wireOp",EDGE,"E246"),sQuery(id+"F0.wireOp",EDGE,"E247"),sQuery(id+"F0.wireOp",EDGE,"E248"),sQuery(id+"F0.wireOp",EDGE,"E249"),sQuery(id+"F0.wireOp",EDGE,"E250"),sQuery(id+"F0.wireOp",EDGE,"E251"),sQuery(id+"F0.wireOp",EDGE,"E252"),sQuery(id+"F0.wireOp",EDGE,"E253"),sQuery(id+"F0.wireOp",EDGE,"E254"),sQuery(id+"F0.wireOp",EDGE,"E255"),sQuery(id+"F0.wireOp",EDGE,"E256"),sQuery(id+"F0.wireOp",EDGE,"E257"),sQuery(id+"F0.wireOp",EDGE,"E258"),sQuery(id+"F0.wireOp",EDGE,"E259"),sQuery(id+"F0.wireOp",EDGE,"E260"),sQuery(id+"F0.wireOp",EDGE,"E261"),sQuery(id+"F0.wireOp",EDGE,"E262"),sQuery(id+"F0.wireOp",EDGE,"E263"),sQuery(id+"F0.wireOp",EDGE,"E264"),sQuery(id+"F0.wireOp",EDGE,"E265"),sQuery(id+"F0.wireOp",EDGE,"E266"),sQuery(id+"F0.wireOp",EDGE,"E267"),sQuery(id+"F0.wireOp",EDGE,"E268"),sQuery(id+"F0.wireOp",EDGE,"E269"),sQuery(id+"F0.wireOp",EDGE,"E270"),sQuery(id+"F0.wireOp",EDGE,"E271"),sQuery(id+"F0.wireOp",EDGE,"E272"),sQuery(id+"F0.wireOp",EDGE,"E273"),sQuery(id+"F0.wireOp",EDGE,"E274"),sQuery(id+"F0.wireOp",EDGE,"E275"),sQuery(id+"F0.wireOp",EDGE,"E276"),sQuery(id+"F0.wireOp",EDGE,"E277"),sQuery(id+"F0.wireOp",EDGE,"E278"),sQuery(id+"F0.wireOp",EDGE,"E279"),sQuery(id+"F0.wireOp",EDGE,"E280"),sQuery(id+"F0.wireOp",EDGE,"E281"),sQuery(id+"F0.wireOp",EDGE,"E282"),sQuery(id+"F0.wireOp",EDGE,"E283"),sQuery(id+"F0.wireOp",EDGE,"E284"),sQuery(id+"F0.wireOp",EDGE,"E285"),sQuery(id+"F0.wireOp",EDGE,"E286"),sQuery(id+"F0.wireOp",EDGE,"E287"),sQuery(id+"F0.wireOp",EDGE,"E288"),sQuery(id+"F0.wireOp",EDGE,"E289"),sQuery(id+"F0.wireOp",EDGE,"E290"),sQuery(id+"F0.wireOp",EDGE,"E291"),sQuery(id+"F0.wireOp",EDGE,"E292"),sQuery(id+"F0.wireOp",EDGE,"E293"),sQuery(id+"F0.wireOp",EDGE,"E294"),sQuery(id+"F0.wireOp",EDGE,"E295"),sQuery(id+"F0.wireOp",EDGE,"E296"),sQuery(id+"F0.wireOp",EDGE,"E297"),sQuery(id+"F0.wireOp",EDGE,"E298"),sQuery(id+"F0.wireOp",EDGE,"E299"),sQuery(id+"F0.wireOp",EDGE,"E300"),sQuery(id+"F0.wireOp",EDGE,"E301"),sQuery(id+"F0.wireOp",EDGE,"E302"),sQuery(id+"F0.wireOp",EDGE,"E303"),sQuery(id+"F0.wireOp",EDGE,"E304"),sQuery(id+"F0.wireOp",EDGE,"E305"),sQuery(id+"F0.wireOp",EDGE,"E306"),sQuery(id+"F0.wireOp",EDGE,"E307"),sQuery(id+"F0.wireOp",EDGE,"E308"),sQuery(id+"F0.wireOp",EDGE,"E309"),sQuery(id+"F0.wireOp",EDGE,"E310"),sQuery(id+"F0.wireOp",EDGE,"E311"),sQuery(id+"F0.wireOp",EDGE,"E312"),sQuery(id+"F0.wireOp",EDGE,"E313"),sQuery(id+"F0.wireOp",EDGE,"E314"),sQuery(id+"F0.wireOp",EDGE,"E315"),sQuery(id+"F0.wireOp",EDGE,"E316"),sQuery(id+"F0.wireOp",EDGE,"E317"),sQuery(id+"F0.wireOp",EDGE,"E318"),sQuery(id+"F0.wireOp",EDGE,"E319"),sQuery(id+"F0.wireOp",EDGE,"E320"),sQuery(id+"F0.wireOp",EDGE,"E321"),sQuery(id+"F0.wireOp",EDGE,"E322"),sQuery(id+"F0.wireOp",EDGE,"E323"),sQuery(id+"F0.wireOp",EDGE,"E324"),sQuery(id+"F0.wireOp",EDGE,"E325"),sQuery(id+"F0.wireOp",EDGE,"E326"),sQuery(id+"F0.wireOp",EDGE,"E327"),sQuery(id+"F0.wireOp",EDGE,"E328"),sQuery(id+"F0.wireOp",EDGE,"E329"),sQuery(id+"F0.wireOp",EDGE,"E330"),sQuery(id+"F0.wireOp",EDGE,"E331"),sQuery(id+"F0.wireOp",EDGE,"E332"),sQuery(id+"F0.wireOp",EDGE,"E333"),sQuery(id+"F0.wireOp",EDGE,"E334"),sQuery(id+"F0.wireOp",EDGE,"E335"),sQuery(id+"F0.wireOp",EDGE,"E336"),sQuery(id+"F0.wireOp",EDGE,"E337"),sQuery(id+"F0.wireOp",EDGE,"E338"),sQuery(id+"F0.wireOp",EDGE,"E339"),sQuery(id+"F0.wireOp",EDGE,"E340"),sQuery(id+"F0.wireOp",EDGE,"E341"),sQuery(id+"F0.wireOp",EDGE,"E342"),sQuery(id+"F0.wireOp",EDGE,"E343"),sQuery(id+"F0.wireOp",EDGE,"E344"),sQuery(id+"F0.wireOp",EDGE,"E345"),sQuery(id+"F0.wireOp",EDGE,"E346"),sQuery(id+"F0.wireOp",EDGE,"E347"),sQuery(id+"F0.wireOp",EDGE,"E348"),sQuery(id+"F0.wireOp",EDGE,"E349"),sQuery(id+"F0.wireOp",EDGE,"E350"),sQuery(id+"F0.wireOp",EDGE,"E351"),sQuery(id+"F0.wireOp",EDGE,"E352"),sQuery(id+"F0.wireOp",EDGE,"E353"),sQuery(id+"F0.wireOp",EDGE,"E354"),sQuery(id+"F0.wireOp",EDGE,"E355"),sQuery(id+"F0.wireOp",EDGE,"E356"),sQuery(id+"F0.wireOp",EDGE,"E357"),sQuery(id+"F0.wireOp",EDGE,"E358"),sQuery(id+"F0.wireOp",EDGE,"E359"),sQuery(id+"F0.wireOp",EDGE,"E360"),sQuery(id+"F0.wireOp",EDGE,"E361"),sQuery(id+"F0.wireOp",EDGE,"E362"),sQuery(id+"F0.wireOp",EDGE,"E363"),sQuery(id+"F0.wireOp",EDGE,"E364"),sQuery(id+"F0.wireOp",EDGE,"E365"),sQuery(id+"F0.wireOp",EDGE,"E366"),sQuery(id+"F0.wireOp",EDGE,"E367"),sQuery(id+"F0.wireOp",EDGE,"E368"),sQuery(id+"F0.wireOp",EDGE,"E369"),sQuery(id+"F0.wireOp",EDGE,"E370"),sQuery(id+"F0.wireOp",EDGE,"E371"),sQuery(id+"F0.wireOp",EDGE,"E372"),sQuery(id+"F0.wireOp",EDGE,"E373"),sQuery(id+"F0.wireOp",EDGE,"E374"),sQuery(id+"F0.wireOp",EDGE,"E375"),sQuery(id+"F0.wireOp",EDGE,"E376"),sQuery(id+"F0.wireOp",EDGE,"E377"),sQuery(id+"F0.wireOp",EDGE,"E378"),sQuery(id+"F0.wireOp",EDGE,"E379"),sQuery(id+"F0.wireOp",EDGE,"E380"),sQuery(id+"F0.wireOp",EDGE,"E381"),sQuery(id+"F0.wireOp",EDGE,"E382"),sQuery(id+"F0.wireOp",EDGE,"E383"),sQuery(id+"F0.wireOp",EDGE,"E384"),sQuery(id+"F0.wireOp",EDGE,"E385"),sQuery(id+"F0.wireOp",EDGE,"E386"),sQuery(id+"F0.wireOp",EDGE,"E387"),sQuery(id+"F0.wireOp",EDGE,"E388"),sQuery(id+"F0.wireOp",EDGE,"E389"),sQuery(id+"F0.wireOp",EDGE,"E390"),sQuery(id+"F0.wireOp",EDGE,"E391"),sQuery(id+"F0.wireOp",EDGE,"E392"),sQuery(id+"F0.wireOp",EDGE,"E393"),sQuery(id+"F0.wireOp",EDGE,"E394"),sQuery(id+"F0.wireOp",EDGE,"E395"),sQuery(id+"F0.wireOp",EDGE,"E396"),sQuery(id+"F0.wireOp",EDGE,"E397"),sQuery(id+"F0.wireOp",EDGE,"E398"),sQuery(id+"F0.wireOp",EDGE,"E399"),sQuery(id+"F0.wireOp",EDGE,"E400"),sQuery(id+"F0.wireOp",EDGE,"E401"),sQuery(id+"F0.wireOp",EDGE,"E402"),sQuery(id+"F0.wireOp",EDGE,"E403"),sQuery(id+"F0.wireOp",EDGE,"E404"),sQuery(id+"F0.wireOp",EDGE,"E405"),sQuery(id+"F0.wireOp",EDGE,"E406"),sQuery(id+"F0.wireOp",EDGE,"E407"),sQuery(id+"F0.wireOp",EDGE,"E408"),sQuery(id+"F0.wireOp",EDGE,"E409"),sQuery(id+"F0.wireOp",EDGE,"E410"),sQuery(id+"F0.wireOp",EDGE,"E411"),sQuery(id+"F0.wireOp",EDGE,"E412"),sQuery(id+"F0.wireOp",EDGE,"E413"),sQuery(id+"F0.wireOp",EDGE,"E414"),sQuery(id+"F0.wireOp",EDGE,"E415"),sQuery(id+"F0.wireOp",EDGE,"E416"),sQuery(id+"F0.wireOp",EDGE,"E417"),sQuery(id+"F0.wireOp",EDGE,"E418"),sQuery(id+"F0.wireOp",EDGE,"E419"),sQuery(id+"F0.wireOp",EDGE,"E420"),sQuery(id+"F0.wireOp",EDGE,"E421"),sQuery(id+"F0.wireOp",EDGE,"E422"),sQuery(id+"F0.wireOp",EDGE,"E423"),sQuery(id+"F0.wireOp",EDGE,"E424"),sQuery(id+"F0.wireOp",EDGE,"E425"),sQuery(id+"F0.wireOp",EDGE,"E426"),sQuery(id+"F0.wireOp",EDGE,"E427"),sQuery(id+"F0.wireOp",EDGE,"E428"),sQuery(id+"F0.wireOp",EDGE,"E429"),sQuery(id+"F0.wireOp",EDGE,"E430"),sQuery(id+"F0.wireOp",EDGE,"E431"),sQuery(id+"F0.wireOp",EDGE,"E432"),sQuery(id+"F0.wireOp",EDGE,"E433"),sQuery(id+"F0.wireOp",EDGE,"E434"),sQuery(id+"F0.wireOp",EDGE,"E435"),sQuery(id+"F0.wireOp",EDGE,"E436"),sQuery(id+"F0.wireOp",EDGE,"E437"),sQuery(id+"F0.wireOp",EDGE,"E438"),sQuery(id+"F0.wireOp",EDGE,"E439"),sQuery(id+"F0.wireOp",EDGE,"E440"),sQuery(id+"F0.wireOp",EDGE,"E441"),sQuery(id+"F0.wireOp",EDGE,"E442"),sQuery(id+"F0.wireOp",EDGE,"E443"),sQuery(id+"F0.wireOp",EDGE,"E444"),sQuery(id+"F0.wireOp",EDGE,"E445"),sQuery(id+"F0.wireOp",EDGE,"E446"),sQuery(id+"F0.wireOp",EDGE,"E447"),sQuery(id+"F0.wireOp",EDGE,"E448"),sQuery(id+"F0.wireOp",EDGE,"E449"),sQuery(id+"F0.wireOp",EDGE,"E450"),sQuery(id+"F0.wireOp",EDGE,"E451"),sQuery(id+"F0.wireOp",EDGE,"E452"),sQuery(id+"F0.wireOp",EDGE,"E453"),sQuery(id+"F0.wireOp",EDGE,"E454"),sQuery(id+"F0.wireOp",EDGE,"E455"),sQuery(id+"F0.wireOp",EDGE,"E456"),sQuery(id+"F0.wireOp",EDGE,"E457"),sQuery(id+"F0.wireOp",EDGE,"E458"),sQuery(id+"F0.wireOp",EDGE,"E459"),sQuery(id+"F0.wireOp",EDGE,"E460"),sQuery(id+"F0.wireOp",EDGE,"E461"),sQuery(id+"F0.wireOp",EDGE,"E462"),sQuery(id+"F0.wireOp",EDGE,"E463"),sQuery(id+"F0.wireOp",EDGE,"E464"),sQuery(id+"F0.wireOp",EDGE,"E465"),sQuery(id+"F0.wireOp",EDGE,"E466"),sQuery(id+"F0.wireOp",EDGE,"E467"),sQuery(id+"F0.wireOp",EDGE,"E468"),sQuery(id+"F0.wireOp",EDGE,"E469"),sQuery(id+"F0.wireOp",EDGE,"E470"),sQuery(id+"F0.wireOp",EDGE,"E471"),sQuery(id+"F0.wireOp",EDGE,"E472"),sQuery(id+"F0.wireOp",EDGE,"E473"),sQuery(id+"F0.wireOp",EDGE,"E474"),sQuery(id+"F0.wireOp",EDGE,"E475"),sQuery(id+"F0.wireOp",EDGE,"E476"),sQuery(id+"F0.wireOp",EDGE,"E477"),sQuery(id+"F0.wireOp",EDGE,"E478"),sQuery(id+"F0.wireOp",EDGE,"E479"),sQuery(id+"F0.wireOp",EDGE,"E480"),sQuery(id+"F0.wireOp",EDGE,"E481"),sQuery(id+"F0.wireOp",EDGE,"E482"),sQuery(id+"F0.wireOp",EDGE,"E483"),sQuery(id+"F0.wireOp",EDGE,"E484"),sQuery(id+"F0.wireOp",EDGE,"E485"),sQuery(id+"F0.wireOp",EDGE,"E486"),sQuery(id+"F0.wireOp",EDGE,"E487"),sQuery(id+"F0.wireOp",EDGE,"E488"),sQuery(id+"F0.wireOp",EDGE,"E489"),sQuery(id+"F0.wireOp",EDGE,"E490"),sQuery(id+"F0.wireOp",EDGE,"E491"),sQuery(id+"F0.wireOp",EDGE,"E492"),sQuery(id+"F0.wireOp",EDGE,"E493"),sQuery(id+"F0.wireOp",EDGE,"E494"),sQuery(id+"F0.wireOp",EDGE,"E495"),sQuery(id+"F0.wireOp",EDGE,"E496"),sQuery(id+"F0.wireOp",EDGE,"E497"),sQuery(id+"F0.wireOp",EDGE,"E498"),sQuery(id+"F0.wireOp",EDGE,"E499"),sQuery(id+"F0.wireOp",EDGE,"E500"),sQuery(id+"F0.wireOp",EDGE,"E501"),sQuery(id+"F0.wireOp",EDGE,"E502"),sQuery(id+"F0.wireOp",EDGE,"E503"),sQuery(id+"F0.wireOp",EDGE,"E504"),sQuery(id+"F0.wireOp",EDGE,"E505"),sQuery(id+"F0.wireOp",EDGE,"E506"),sQuery(id+"F0.wireOp",EDGE,"E507"),sQuery(id+"F0.wireOp",EDGE,"E508"),sQuery(id+"F0.wireOp",EDGE,"E509"),sQuery(id+"F0.wireOp",EDGE,"E510"),sQuery(id+"F0.wireOp",EDGE,"E511"),sQuery(id+"F0.wireOp",EDGE,"E512"),sQuery(id+"F0.wireOp",EDGE,"E513"),sQuery(id+"F0.wireOp",EDGE,"E514"),sQuery(id+"F0.wireOp",EDGE,"E515"),sQuery(id+"F0.wireOp",EDGE,"E516"),sQuery(id+"F0.wireOp",EDGE,"E517"),sQuery(id+"F0.wireOp",EDGE,"E518"),sQuery(id+"F0.wireOp",EDGE,"E519"),sQuery(id+"F0.wireOp",EDGE,"E520"),sQuery(id+"F0.wireOp",EDGE,"E521"),sQuery(id+"F0.wireOp",EDGE,"E522"),sQuery(id+"F0.wireOp",EDGE,"E523"),sQuery(id+"F0.wireOp",EDGE,"E524"),sQuery(id+"F0.wireOp",EDGE,"E525"),sQuery(id+"F0.wireOp",EDGE,"E526"),sQuery(id+"F0.wireOp",EDGE,"E527"),sQuery(id+"F0.wireOp",EDGE,"E528"),sQuery(id+"F0.wireOp",EDGE,"E529"),sQuery(id+"F0.wireOp",EDGE,"E530"),sQuery(id+"F0.wireOp",EDGE,"E531"),sQuery(id+"F0.wireOp",EDGE,"E532"),sQuery(id+"F0.wireOp",EDGE,"E533"),sQuery(id+"F0.wireOp",EDGE,"E534"),sQuery(id+"F0.wireOp",EDGE,"E535"),sQuery(id+"F0.wireOp",EDGE,"E536"),sQuery(id+"F0.wireOp",EDGE,"E537"),sQuery(id+"F0.wireOp",EDGE,"E538"),sQuery(id+"F0.wireOp",EDGE,"E539"),sQuery(id+"F0.wireOp",EDGE,"E540"),sQuery(id+"F0.wireOp",EDGE,"E541"),sQuery(id+"F0.wireOp",EDGE,"E542"),sQuery(id+"F0.wireOp",EDGE,"E543"),sQuery(id+"F0.wireOp",EDGE,"E544"),sQuery(id+"F0.wireOp",EDGE,"E545"),sQuery(id+"F0.wireOp",EDGE,"E546"),sQuery(id+"F0.wireOp",EDGE,"E547"),sQuery(id+"F0.wireOp",EDGE,"E548"),sQuery(id+"F0.wireOp",EDGE,"E549"),sQuery(id+"F0.wireOp",EDGE,"E550"),sQuery(id+"F0.wireOp",EDGE,"E551"),sQuery(id+"F0.wireOp",EDGE,"E552"),sQuery(id+"F0.wireOp",EDGE,"E553"),sQuery(id+"F0.wireOp",EDGE,"E554"),sQuery(id+"F0.wireOp",EDGE,"E555"),sQuery(id+"F0.wireOp",EDGE,"E556"),sQuery(id+"F0.wireOp",EDGE,"E557"),sQuery(id+"F0.wireOp",EDGE,"E558"),sQuery(id+"F0.wireOp",EDGE,"E559"),sQuery(id+"F0.wireOp",EDGE,"E560"),sQuery(id+"F0.wireOp",EDGE,"E561"),sQuery(id+"F0.wireOp",EDGE,"E562"),sQuery(id+"F0.wireOp",EDGE,"E563")])],"isStart":false});
            var sketch = newSketch(context, id + "F2", { "sketchPlane" : qUnion([Q0])});
            skCircle(sketch, "E564", {"center": v(-2.86, 0) * mm, "radius": 9.5 * mm});
            skSolve(sketch);
        }
        {
            var Q0;
            Q0=makeQuery(id+"F2.imprint","IMPRINT",FACE,{"disambiguationData":[TD([[makeQuery(id+"F2.imprint","IMPRINT",EDGE,{"derivedFrom":sQuery(id+"F2.wireOp",EDGE,"E564")}),1.0]])]});
            extrude(context, id + "F3", {"entities" : qUnion([Q0]), "operationType" : NewBodyOperationType.ADD, "depth" : 1 * mm});
        }
        {
            var Q0;
            Q0=makeQuery(id+"F3.opExtrude","CAP_EDGE",EDGE,{"disambiguationData":[OSD([sQuery(id+"F2.wireOp",EDGE,"E564")])],"isStart":false});
            fillet(context, id + "F4", {"entities" : qUnion([Q0]), "radius" : 0.4 * mm, "tangentPropagation" : true, "allowEdgeOverflow" : false});
        }
    });
